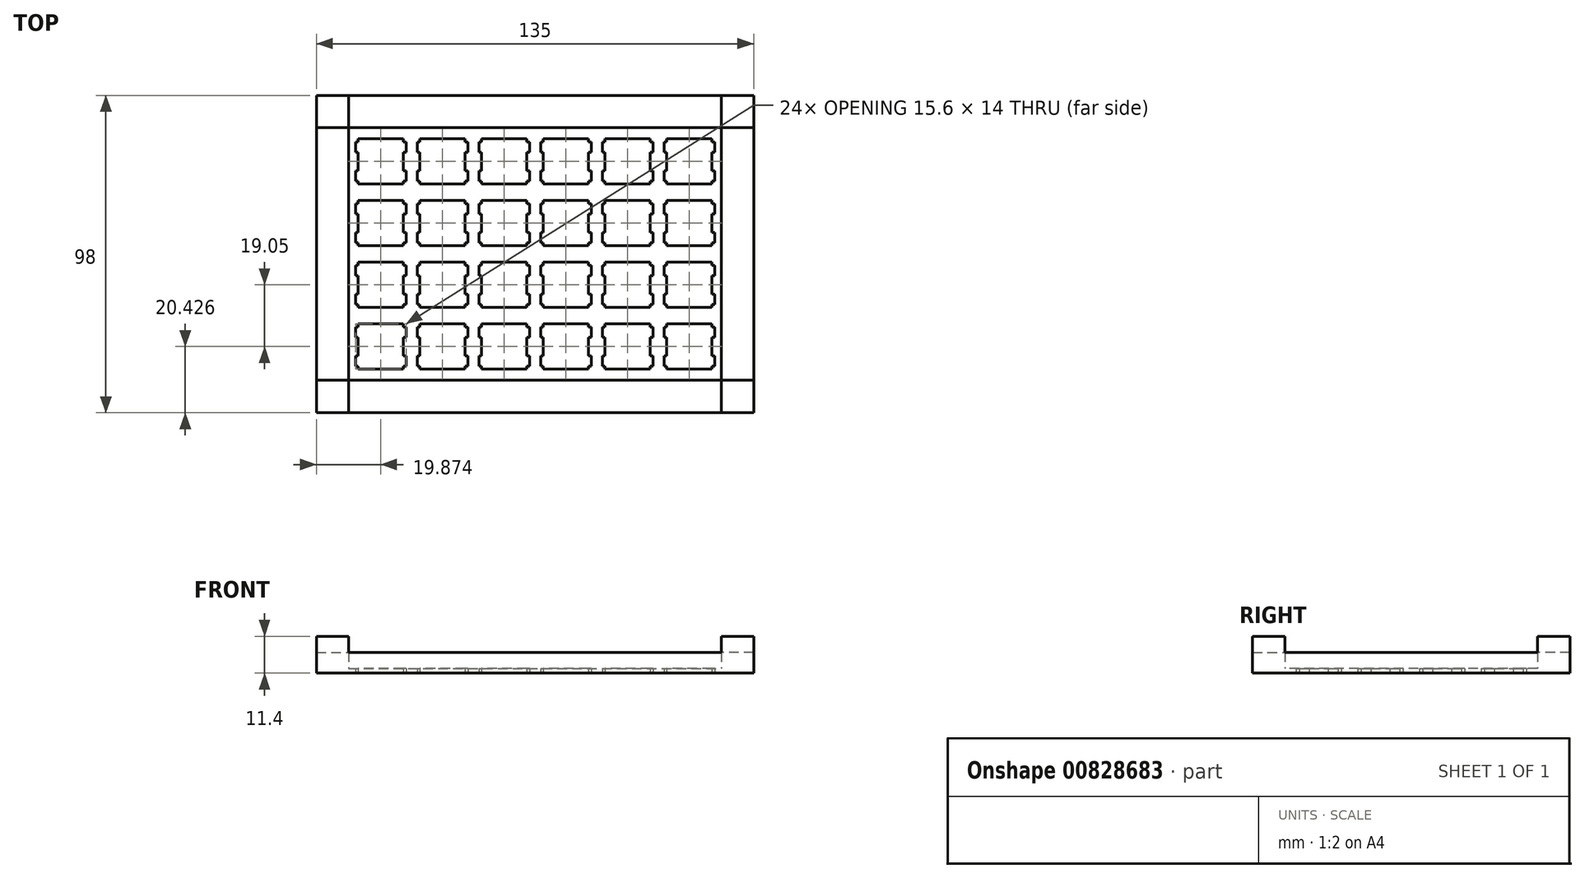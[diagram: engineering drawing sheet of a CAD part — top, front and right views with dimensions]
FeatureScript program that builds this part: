
annotation { "Feature Type Name" : "Feature", "Feature Type Description" : "" }
export const myFeature = defineFeature(function(context is Context, id is Id, definition is map)
    precondition{}
    {
        {
            var Q0;
            Q0=qCreatedBy(makeId("Top.planeOp"),FACE);
            var sketch = newSketch(context, id + "F0", { "sketchPlane" : qUnion([Q0])});
            skLineSegment(sketch, "E0", {"start": v(-60.15, 41.1) * mm, "end": v(60.15, 41.1) * mm});
            skLineSegment(sketch, "E1", {"start": v(60.15, 41.1) * mm, "end": v(60.15, -41.1) * mm});
            skLineSegment(sketch, "E2", {"start": v(60.15, -41.1) * mm, "end": v(-60.15, -41.1) * mm});
            skLineSegment(sketch, "E3", {"start": v(-60.15, -41.1) * mm, "end": v(-60.15, 41.1) * mm});
            skLineSegment(sketch, "E4", {"start": v(-54.63, -21.57) * mm, "end": v(-54.63, -22.57) * mm});
            skLineSegment(sketch, "E5", {"start": v(-54.63, -22.57) * mm, "end": v(-55.43, -22.57) * mm});
            skLineSegment(sketch, "E6", {"start": v(-55.43, -22.57) * mm, "end": v(-55.43, -25.67) * mm});
            skLineSegment(sketch, "E7", {"start": v(-55.43, -25.67) * mm, "end": v(-54.63, -25.67) * mm});
            skLineSegment(sketch, "E8", {"start": v(-54.63, -25.67) * mm, "end": v(-54.63, -31.47) * mm});
            skLineSegment(sketch, "E9", {"start": v(-54.63, -31.47) * mm, "end": v(-55.43, -31.47) * mm});
            skLineSegment(sketch, "E10", {"start": v(-55.43, -31.47) * mm, "end": v(-55.43, -34.57) * mm});
            skLineSegment(sketch, "E11", {"start": v(-55.43, -34.57) * mm, "end": v(-54.63, -34.57) * mm});
            skLineSegment(sketch, "E12", {"start": v(-54.63, -34.57) * mm, "end": v(-54.63, -35.57) * mm});
            skLineSegment(sketch, "E13", {"start": v(-54.63, -35.57) * mm, "end": v(-40.62, -35.57) * mm});
            skLineSegment(sketch, "E14", {"start": v(-40.62, -35.57) * mm, "end": v(-40.62, -34.57) * mm});
            skLineSegment(sketch, "E15", {"start": v(-40.62, -34.57) * mm, "end": v(-39.83, -34.57) * mm});
            skLineSegment(sketch, "E16", {"start": v(-39.83, -34.57) * mm, "end": v(-39.83, -31.47) * mm});
            skLineSegment(sketch, "E17", {"start": v(-39.83, -31.47) * mm, "end": v(-40.62, -31.47) * mm});
            skLineSegment(sketch, "E18", {"start": v(-40.62, -31.47) * mm, "end": v(-40.62, -25.67) * mm});
            skLineSegment(sketch, "E19", {"start": v(-40.62, -25.67) * mm, "end": v(-39.83, -25.67) * mm});
            skLineSegment(sketch, "E20", {"start": v(-39.83, -25.67) * mm, "end": v(-39.83, -22.57) * mm});
            skLineSegment(sketch, "E21", {"start": v(-39.83, -22.57) * mm, "end": v(-40.62, -22.57) * mm});
            skLineSegment(sketch, "E22", {"start": v(-40.62, -22.57) * mm, "end": v(-40.62, -21.57) * mm});
            skLineSegment(sketch, "E23", {"start": v(-40.62, -21.57) * mm, "end": v(-54.63, -21.57) * mm});
            skLineSegment(sketch, "E24", {"start": v(-35.58, -21.57) * mm, "end": v(-35.58, -22.57) * mm});
            skLineSegment(sketch, "E25", {"start": v(-35.58, -22.57) * mm, "end": v(-36.37, -22.57) * mm});
            skLineSegment(sketch, "E26", {"start": v(-36.37, -22.57) * mm, "end": v(-36.37, -25.67) * mm});
            skLineSegment(sketch, "E27", {"start": v(-36.37, -25.67) * mm, "end": v(-35.58, -25.67) * mm});
            skLineSegment(sketch, "E28", {"start": v(-35.58, -25.67) * mm, "end": v(-35.58, -31.47) * mm});
            skLineSegment(sketch, "E29", {"start": v(-35.58, -31.47) * mm, "end": v(-36.37, -31.47) * mm});
            skLineSegment(sketch, "E30", {"start": v(-36.37, -31.47) * mm, "end": v(-36.37, -34.57) * mm});
            skLineSegment(sketch, "E31", {"start": v(-36.37, -34.57) * mm, "end": v(-35.58, -34.57) * mm});
            skLineSegment(sketch, "E32", {"start": v(-35.58, -34.57) * mm, "end": v(-35.58, -35.57) * mm});
            skLineSegment(sketch, "E33", {"start": v(-35.58, -35.57) * mm, "end": v(-21.57, -35.57) * mm});
            skLineSegment(sketch, "E34", {"start": v(-21.57, -35.57) * mm, "end": v(-21.57, -34.57) * mm});
            skLineSegment(sketch, "E35", {"start": v(-21.57, -34.57) * mm, "end": v(-20.78, -34.57) * mm});
            skLineSegment(sketch, "E36", {"start": v(-20.78, -34.57) * mm, "end": v(-20.78, -31.47) * mm});
            skLineSegment(sketch, "E37", {"start": v(-20.78, -31.47) * mm, "end": v(-21.57, -31.47) * mm});
            skLineSegment(sketch, "E38", {"start": v(-21.57, -31.47) * mm, "end": v(-21.57, -25.67) * mm});
            skLineSegment(sketch, "E39", {"start": v(-21.57, -25.67) * mm, "end": v(-20.78, -25.67) * mm});
            skLineSegment(sketch, "E40", {"start": v(-20.78, -25.67) * mm, "end": v(-20.78, -22.57) * mm});
            skLineSegment(sketch, "E41", {"start": v(-20.78, -22.57) * mm, "end": v(-21.57, -22.57) * mm});
            skLineSegment(sketch, "E42", {"start": v(-21.57, -22.57) * mm, "end": v(-21.57, -21.57) * mm});
            skLineSegment(sketch, "E43", {"start": v(-21.57, -21.57) * mm, "end": v(-35.58, -21.57) * mm});
            skLineSegment(sketch, "E44", {"start": v(-16.53, -21.57) * mm, "end": v(-16.53, -22.57) * mm});
            skLineSegment(sketch, "E45", {"start": v(-16.53, -22.57) * mm, "end": v(-17.32, -22.57) * mm});
            skLineSegment(sketch, "E46", {"start": v(-17.32, -22.57) * mm, "end": v(-17.32, -25.67) * mm});
            skLineSegment(sketch, "E47", {"start": v(-17.32, -25.67) * mm, "end": v(-16.53, -25.67) * mm});
            skLineSegment(sketch, "E48", {"start": v(-16.53, -25.67) * mm, "end": v(-16.53, -31.47) * mm});
            skLineSegment(sketch, "E49", {"start": v(-16.53, -31.47) * mm, "end": v(-17.32, -31.47) * mm});
            skLineSegment(sketch, "E50", {"start": v(-17.32, -31.47) * mm, "end": v(-17.32, -34.57) * mm});
            skLineSegment(sketch, "E51", {"start": v(-17.32, -34.57) * mm, "end": v(-16.53, -34.57) * mm});
            skLineSegment(sketch, "E52", {"start": v(-16.53, -34.57) * mm, "end": v(-16.53, -35.57) * mm});
            skLineSegment(sketch, "E53", {"start": v(-16.53, -35.57) * mm, "end": v(-2.52, -35.57) * mm});
            skLineSegment(sketch, "E54", {"start": v(-2.52, -35.57) * mm, "end": v(-2.52, -34.57) * mm});
            skLineSegment(sketch, "E55", {"start": v(-2.52, -34.57) * mm, "end": v(-1.73, -34.57) * mm});
            skLineSegment(sketch, "E56", {"start": v(-1.73, -34.57) * mm, "end": v(-1.73, -31.47) * mm});
            skLineSegment(sketch, "E57", {"start": v(-1.73, -31.47) * mm, "end": v(-2.52, -31.47) * mm});
            skLineSegment(sketch, "E58", {"start": v(-2.52, -31.47) * mm, "end": v(-2.52, -25.67) * mm});
            skLineSegment(sketch, "E59", {"start": v(-2.52, -25.67) * mm, "end": v(-1.73, -25.67) * mm});
            skLineSegment(sketch, "E60", {"start": v(-1.73, -25.67) * mm, "end": v(-1.73, -22.57) * mm});
            skLineSegment(sketch, "E61", {"start": v(-1.73, -22.57) * mm, "end": v(-2.52, -22.57) * mm});
            skLineSegment(sketch, "E62", {"start": v(-2.52, -22.57) * mm, "end": v(-2.52, -21.57) * mm});
            skLineSegment(sketch, "E63", {"start": v(-2.52, -21.57) * mm, "end": v(-16.53, -21.57) * mm});
            skLineSegment(sketch, "E64", {"start": v(2.52, -21.57) * mm, "end": v(2.52, -22.57) * mm});
            skLineSegment(sketch, "E65", {"start": v(2.52, -22.57) * mm, "end": v(1.73, -22.57) * mm});
            skLineSegment(sketch, "E66", {"start": v(1.73, -22.57) * mm, "end": v(1.73, -25.67) * mm});
            skLineSegment(sketch, "E67", {"start": v(1.73, -25.67) * mm, "end": v(2.52, -25.67) * mm});
            skLineSegment(sketch, "E68", {"start": v(2.52, -25.67) * mm, "end": v(2.52, -31.47) * mm});
            skLineSegment(sketch, "E69", {"start": v(2.52, -31.47) * mm, "end": v(1.73, -31.47) * mm});
            skLineSegment(sketch, "E70", {"start": v(1.73, -31.47) * mm, "end": v(1.73, -34.57) * mm});
            skLineSegment(sketch, "E71", {"start": v(1.73, -34.57) * mm, "end": v(2.52, -34.57) * mm});
            skLineSegment(sketch, "E72", {"start": v(2.52, -34.57) * mm, "end": v(2.52, -35.57) * mm});
            skLineSegment(sketch, "E73", {"start": v(2.52, -35.57) * mm, "end": v(16.53, -35.57) * mm});
            skLineSegment(sketch, "E74", {"start": v(16.53, -35.57) * mm, "end": v(16.53, -34.57) * mm});
            skLineSegment(sketch, "E75", {"start": v(16.53, -34.57) * mm, "end": v(17.32, -34.57) * mm});
            skLineSegment(sketch, "E76", {"start": v(17.32, -34.57) * mm, "end": v(17.32, -31.47) * mm});
            skLineSegment(sketch, "E77", {"start": v(17.32, -31.47) * mm, "end": v(16.53, -31.47) * mm});
            skLineSegment(sketch, "E78", {"start": v(16.53, -31.47) * mm, "end": v(16.53, -25.67) * mm});
            skLineSegment(sketch, "E79", {"start": v(16.53, -25.67) * mm, "end": v(17.32, -25.67) * mm});
            skLineSegment(sketch, "E80", {"start": v(17.32, -25.67) * mm, "end": v(17.32, -22.57) * mm});
            skLineSegment(sketch, "E81", {"start": v(17.32, -22.57) * mm, "end": v(16.53, -22.57) * mm});
            skLineSegment(sketch, "E82", {"start": v(16.53, -22.57) * mm, "end": v(16.53, -21.57) * mm});
            skLineSegment(sketch, "E83", {"start": v(16.53, -21.57) * mm, "end": v(2.52, -21.57) * mm});
            skLineSegment(sketch, "E84", {"start": v(21.57, -21.57) * mm, "end": v(21.57, -22.57) * mm});
            skLineSegment(sketch, "E85", {"start": v(21.57, -22.57) * mm, "end": v(20.78, -22.57) * mm});
            skLineSegment(sketch, "E86", {"start": v(20.78, -22.57) * mm, "end": v(20.78, -25.67) * mm});
            skLineSegment(sketch, "E87", {"start": v(20.78, -25.67) * mm, "end": v(21.57, -25.67) * mm});
            skLineSegment(sketch, "E88", {"start": v(21.57, -25.67) * mm, "end": v(21.57, -31.47) * mm});
            skLineSegment(sketch, "E89", {"start": v(21.57, -31.47) * mm, "end": v(20.78, -31.47) * mm});
            skLineSegment(sketch, "E90", {"start": v(20.78, -31.47) * mm, "end": v(20.78, -34.57) * mm});
            skLineSegment(sketch, "E91", {"start": v(20.78, -34.57) * mm, "end": v(21.57, -34.57) * mm});
            skLineSegment(sketch, "E92", {"start": v(21.57, -34.57) * mm, "end": v(21.57, -35.57) * mm});
            skLineSegment(sketch, "E93", {"start": v(21.57, -35.57) * mm, "end": v(35.58, -35.57) * mm});
            skLineSegment(sketch, "E94", {"start": v(35.58, -35.57) * mm, "end": v(35.58, -34.57) * mm});
            skLineSegment(sketch, "E95", {"start": v(35.58, -34.57) * mm, "end": v(36.37, -34.57) * mm});
            skLineSegment(sketch, "E96", {"start": v(36.37, -34.57) * mm, "end": v(36.37, -31.47) * mm});
            skLineSegment(sketch, "E97", {"start": v(36.37, -31.47) * mm, "end": v(35.58, -31.47) * mm});
            skLineSegment(sketch, "E98", {"start": v(35.58, -31.47) * mm, "end": v(35.58, -25.67) * mm});
            skLineSegment(sketch, "E99", {"start": v(35.58, -25.67) * mm, "end": v(36.37, -25.67) * mm});
            skLineSegment(sketch, "E100", {"start": v(36.37, -25.67) * mm, "end": v(36.37, -22.57) * mm});
            skLineSegment(sketch, "E101", {"start": v(36.37, -22.57) * mm, "end": v(35.58, -22.57) * mm});
            skLineSegment(sketch, "E102", {"start": v(35.58, -22.57) * mm, "end": v(35.58, -21.57) * mm});
            skLineSegment(sketch, "E103", {"start": v(35.58, -21.57) * mm, "end": v(21.57, -21.57) * mm});
            skLineSegment(sketch, "E104", {"start": v(40.62, -21.57) * mm, "end": v(40.62, -22.57) * mm});
            skLineSegment(sketch, "E105", {"start": v(40.62, -22.57) * mm, "end": v(39.83, -22.57) * mm});
            skLineSegment(sketch, "E106", {"start": v(39.83, -22.57) * mm, "end": v(39.83, -25.67) * mm});
            skLineSegment(sketch, "E107", {"start": v(39.83, -25.67) * mm, "end": v(40.62, -25.67) * mm});
            skLineSegment(sketch, "E108", {"start": v(40.62, -25.67) * mm, "end": v(40.62, -31.47) * mm});
            skLineSegment(sketch, "E109", {"start": v(40.62, -31.47) * mm, "end": v(39.83, -31.47) * mm});
            skLineSegment(sketch, "E110", {"start": v(39.83, -31.47) * mm, "end": v(39.83, -34.57) * mm});
            skLineSegment(sketch, "E111", {"start": v(39.83, -34.57) * mm, "end": v(40.62, -34.57) * mm});
            skLineSegment(sketch, "E112", {"start": v(40.62, -34.57) * mm, "end": v(40.62, -35.57) * mm});
            skLineSegment(sketch, "E113", {"start": v(40.62, -35.57) * mm, "end": v(54.62, -35.57) * mm});
            skLineSegment(sketch, "E114", {"start": v(54.62, -35.57) * mm, "end": v(54.62, -34.57) * mm});
            skLineSegment(sketch, "E115", {"start": v(54.62, -34.57) * mm, "end": v(55.42, -34.57) * mm});
            skLineSegment(sketch, "E116", {"start": v(55.42, -34.57) * mm, "end": v(55.42, -31.47) * mm});
            skLineSegment(sketch, "E117", {"start": v(55.42, -31.47) * mm, "end": v(54.62, -31.47) * mm});
            skLineSegment(sketch, "E118", {"start": v(54.62, -31.47) * mm, "end": v(54.62, -25.67) * mm});
            skLineSegment(sketch, "E119", {"start": v(54.62, -25.67) * mm, "end": v(55.42, -25.67) * mm});
            skLineSegment(sketch, "E120", {"start": v(55.42, -25.67) * mm, "end": v(55.42, -22.57) * mm});
            skLineSegment(sketch, "E121", {"start": v(55.42, -22.57) * mm, "end": v(54.62, -22.57) * mm});
            skLineSegment(sketch, "E122", {"start": v(54.62, -22.57) * mm, "end": v(54.62, -21.57) * mm});
            skLineSegment(sketch, "E123", {"start": v(54.62, -21.57) * mm, "end": v(40.62, -21.57) * mm});
            skLineSegment(sketch, "E124", {"start": v(-54.63, -2.52) * mm, "end": v(-54.63, -3.52) * mm});
            skLineSegment(sketch, "E125", {"start": v(-54.63, -3.52) * mm, "end": v(-55.43, -3.52) * mm});
            skLineSegment(sketch, "E126", {"start": v(-55.43, -3.52) * mm, "end": v(-55.43, -6.62) * mm});
            skLineSegment(sketch, "E127", {"start": v(-55.43, -6.62) * mm, "end": v(-54.63, -6.62) * mm});
            skLineSegment(sketch, "E128", {"start": v(-54.63, -6.62) * mm, "end": v(-54.63, -12.42) * mm});
            skLineSegment(sketch, "E129", {"start": v(-54.63, -12.42) * mm, "end": v(-55.43, -12.42) * mm});
            skLineSegment(sketch, "E130", {"start": v(-55.43, -12.42) * mm, "end": v(-55.43, -15.52) * mm});
            skLineSegment(sketch, "E131", {"start": v(-55.43, -15.52) * mm, "end": v(-54.63, -15.52) * mm});
            skLineSegment(sketch, "E132", {"start": v(-54.63, -15.52) * mm, "end": v(-54.63, -16.52) * mm});
            skLineSegment(sketch, "E133", {"start": v(-54.63, -16.52) * mm, "end": v(-40.62, -16.52) * mm});
            skLineSegment(sketch, "E134", {"start": v(-40.62, -16.52) * mm, "end": v(-40.62, -15.52) * mm});
            skLineSegment(sketch, "E135", {"start": v(-40.62, -15.52) * mm, "end": v(-39.83, -15.52) * mm});
            skLineSegment(sketch, "E136", {"start": v(-39.83, -15.52) * mm, "end": v(-39.83, -12.42) * mm});
            skLineSegment(sketch, "E137", {"start": v(-39.83, -12.42) * mm, "end": v(-40.62, -12.42) * mm});
            skLineSegment(sketch, "E138", {"start": v(-40.62, -12.42) * mm, "end": v(-40.62, -6.62) * mm});
            skLineSegment(sketch, "E139", {"start": v(-40.62, -6.62) * mm, "end": v(-39.83, -6.62) * mm});
            skLineSegment(sketch, "E140", {"start": v(-39.83, -6.62) * mm, "end": v(-39.83, -3.52) * mm});
            skLineSegment(sketch, "E141", {"start": v(-39.83, -3.52) * mm, "end": v(-40.62, -3.52) * mm});
            skLineSegment(sketch, "E142", {"start": v(-40.62, -3.52) * mm, "end": v(-40.62, -2.52) * mm});
            skLineSegment(sketch, "E143", {"start": v(-40.62, -2.52) * mm, "end": v(-54.63, -2.52) * mm});
            skLineSegment(sketch, "E144", {"start": v(-35.58, -2.52) * mm, "end": v(-35.58, -3.52) * mm});
            skLineSegment(sketch, "E145", {"start": v(-35.58, -3.52) * mm, "end": v(-36.37, -3.52) * mm});
            skLineSegment(sketch, "E146", {"start": v(-36.37, -3.52) * mm, "end": v(-36.37, -6.62) * mm});
            skLineSegment(sketch, "E147", {"start": v(-36.37, -6.62) * mm, "end": v(-35.58, -6.62) * mm});
            skLineSegment(sketch, "E148", {"start": v(-35.58, -6.62) * mm, "end": v(-35.58, -12.42) * mm});
            skLineSegment(sketch, "E149", {"start": v(-35.58, -12.42) * mm, "end": v(-36.37, -12.42) * mm});
            skLineSegment(sketch, "E150", {"start": v(-36.37, -12.42) * mm, "end": v(-36.37, -15.52) * mm});
            skLineSegment(sketch, "E151", {"start": v(-36.37, -15.52) * mm, "end": v(-35.58, -15.52) * mm});
            skLineSegment(sketch, "E152", {"start": v(-35.58, -15.52) * mm, "end": v(-35.58, -16.52) * mm});
            skLineSegment(sketch, "E153", {"start": v(-35.58, -16.52) * mm, "end": v(-21.57, -16.52) * mm});
            skLineSegment(sketch, "E154", {"start": v(-21.57, -16.52) * mm, "end": v(-21.57, -15.52) * mm});
            skLineSegment(sketch, "E155", {"start": v(-21.57, -15.52) * mm, "end": v(-20.78, -15.52) * mm});
            skLineSegment(sketch, "E156", {"start": v(-20.78, -15.52) * mm, "end": v(-20.78, -12.42) * mm});
            skLineSegment(sketch, "E157", {"start": v(-20.78, -12.42) * mm, "end": v(-21.57, -12.42) * mm});
            skLineSegment(sketch, "E158", {"start": v(-21.57, -12.42) * mm, "end": v(-21.57, -6.62) * mm});
            skLineSegment(sketch, "E159", {"start": v(-21.57, -6.62) * mm, "end": v(-20.78, -6.62) * mm});
            skLineSegment(sketch, "E160", {"start": v(-20.78, -6.62) * mm, "end": v(-20.78, -3.52) * mm});
            skLineSegment(sketch, "E161", {"start": v(-20.78, -3.52) * mm, "end": v(-21.57, -3.52) * mm});
            skLineSegment(sketch, "E162", {"start": v(-21.57, -3.52) * mm, "end": v(-21.57, -2.52) * mm});
            skLineSegment(sketch, "E163", {"start": v(-21.57, -2.52) * mm, "end": v(-35.58, -2.52) * mm});
            skLineSegment(sketch, "E164", {"start": v(-16.53, -2.52) * mm, "end": v(-16.53, -3.52) * mm});
            skLineSegment(sketch, "E165", {"start": v(-16.53, -3.52) * mm, "end": v(-17.32, -3.52) * mm});
            skLineSegment(sketch, "E166", {"start": v(-17.32, -3.52) * mm, "end": v(-17.32, -6.62) * mm});
            skLineSegment(sketch, "E167", {"start": v(-17.32, -6.62) * mm, "end": v(-16.53, -6.62) * mm});
            skLineSegment(sketch, "E168", {"start": v(-16.53, -6.62) * mm, "end": v(-16.53, -12.42) * mm});
            skLineSegment(sketch, "E169", {"start": v(-16.53, -12.42) * mm, "end": v(-17.32, -12.42) * mm});
            skLineSegment(sketch, "E170", {"start": v(-17.32, -12.42) * mm, "end": v(-17.32, -15.52) * mm});
            skLineSegment(sketch, "E171", {"start": v(-17.32, -15.52) * mm, "end": v(-16.53, -15.52) * mm});
            skLineSegment(sketch, "E172", {"start": v(-16.53, -15.52) * mm, "end": v(-16.53, -16.52) * mm});
            skLineSegment(sketch, "E173", {"start": v(-16.53, -16.52) * mm, "end": v(-2.52, -16.52) * mm});
            skLineSegment(sketch, "E174", {"start": v(-2.52, -16.52) * mm, "end": v(-2.52, -15.52) * mm});
            skLineSegment(sketch, "E175", {"start": v(-2.52, -15.52) * mm, "end": v(-1.73, -15.52) * mm});
            skLineSegment(sketch, "E176", {"start": v(-1.73, -15.52) * mm, "end": v(-1.73, -12.42) * mm});
            skLineSegment(sketch, "E177", {"start": v(-1.73, -12.42) * mm, "end": v(-2.52, -12.42) * mm});
            skLineSegment(sketch, "E178", {"start": v(-2.52, -12.42) * mm, "end": v(-2.52, -6.62) * mm});
            skLineSegment(sketch, "E179", {"start": v(-2.52, -6.62) * mm, "end": v(-1.73, -6.62) * mm});
            skLineSegment(sketch, "E180", {"start": v(-1.73, -6.62) * mm, "end": v(-1.73, -3.52) * mm});
            skLineSegment(sketch, "E181", {"start": v(-1.73, -3.52) * mm, "end": v(-2.52, -3.52) * mm});
            skLineSegment(sketch, "E182", {"start": v(-2.52, -3.52) * mm, "end": v(-2.52, -2.52) * mm});
            skLineSegment(sketch, "E183", {"start": v(-2.52, -2.52) * mm, "end": v(-16.53, -2.52) * mm});
            skLineSegment(sketch, "E184", {"start": v(2.52, -2.52) * mm, "end": v(2.52, -3.52) * mm});
            skLineSegment(sketch, "E185", {"start": v(2.52, -3.52) * mm, "end": v(1.73, -3.52) * mm});
            skLineSegment(sketch, "E186", {"start": v(1.73, -3.52) * mm, "end": v(1.73, -6.62) * mm});
            skLineSegment(sketch, "E187", {"start": v(1.73, -6.62) * mm, "end": v(2.52, -6.62) * mm});
            skLineSegment(sketch, "E188", {"start": v(2.52, -6.62) * mm, "end": v(2.52, -12.42) * mm});
            skLineSegment(sketch, "E189", {"start": v(2.52, -12.42) * mm, "end": v(1.73, -12.42) * mm});
            skLineSegment(sketch, "E190", {"start": v(1.73, -12.42) * mm, "end": v(1.73, -15.52) * mm});
            skLineSegment(sketch, "E191", {"start": v(1.73, -15.52) * mm, "end": v(2.52, -15.52) * mm});
            skLineSegment(sketch, "E192", {"start": v(2.52, -15.52) * mm, "end": v(2.52, -16.52) * mm});
            skLineSegment(sketch, "E193", {"start": v(2.52, -16.52) * mm, "end": v(16.53, -16.52) * mm});
            skLineSegment(sketch, "E194", {"start": v(16.53, -16.52) * mm, "end": v(16.53, -15.52) * mm});
            skLineSegment(sketch, "E195", {"start": v(16.53, -15.52) * mm, "end": v(17.32, -15.52) * mm});
            skLineSegment(sketch, "E196", {"start": v(17.32, -15.52) * mm, "end": v(17.32, -12.42) * mm});
            skLineSegment(sketch, "E197", {"start": v(17.32, -12.42) * mm, "end": v(16.53, -12.42) * mm});
            skLineSegment(sketch, "E198", {"start": v(16.53, -12.42) * mm, "end": v(16.53, -6.62) * mm});
            skLineSegment(sketch, "E199", {"start": v(16.53, -6.62) * mm, "end": v(17.32, -6.62) * mm});
            skLineSegment(sketch, "E200", {"start": v(17.32, -6.62) * mm, "end": v(17.32, -3.52) * mm});
            skLineSegment(sketch, "E201", {"start": v(17.32, -3.52) * mm, "end": v(16.53, -3.52) * mm});
            skLineSegment(sketch, "E202", {"start": v(16.53, -3.52) * mm, "end": v(16.53, -2.52) * mm});
            skLineSegment(sketch, "E203", {"start": v(16.53, -2.52) * mm, "end": v(2.52, -2.52) * mm});
            skLineSegment(sketch, "E204", {"start": v(21.57, -2.52) * mm, "end": v(21.57, -3.52) * mm});
            skLineSegment(sketch, "E205", {"start": v(21.57, -3.52) * mm, "end": v(20.78, -3.52) * mm});
            skLineSegment(sketch, "E206", {"start": v(20.78, -3.52) * mm, "end": v(20.78, -6.62) * mm});
            skLineSegment(sketch, "E207", {"start": v(20.78, -6.62) * mm, "end": v(21.57, -6.62) * mm});
            skLineSegment(sketch, "E208", {"start": v(21.57, -6.62) * mm, "end": v(21.57, -12.42) * mm});
            skLineSegment(sketch, "E209", {"start": v(21.57, -12.42) * mm, "end": v(20.78, -12.42) * mm});
            skLineSegment(sketch, "E210", {"start": v(20.78, -12.42) * mm, "end": v(20.78, -15.52) * mm});
            skLineSegment(sketch, "E211", {"start": v(20.78, -15.52) * mm, "end": v(21.57, -15.52) * mm});
            skLineSegment(sketch, "E212", {"start": v(21.57, -15.52) * mm, "end": v(21.57, -16.52) * mm});
            skLineSegment(sketch, "E213", {"start": v(21.57, -16.52) * mm, "end": v(35.58, -16.52) * mm});
            skLineSegment(sketch, "E214", {"start": v(35.58, -16.52) * mm, "end": v(35.58, -15.52) * mm});
            skLineSegment(sketch, "E215", {"start": v(35.58, -15.52) * mm, "end": v(36.37, -15.52) * mm});
            skLineSegment(sketch, "E216", {"start": v(36.37, -15.52) * mm, "end": v(36.37, -12.42) * mm});
            skLineSegment(sketch, "E217", {"start": v(36.37, -12.42) * mm, "end": v(35.58, -12.42) * mm});
            skLineSegment(sketch, "E218", {"start": v(35.58, -12.42) * mm, "end": v(35.58, -6.62) * mm});
            skLineSegment(sketch, "E219", {"start": v(35.58, -6.62) * mm, "end": v(36.37, -6.62) * mm});
            skLineSegment(sketch, "E220", {"start": v(36.37, -6.62) * mm, "end": v(36.37, -3.52) * mm});
            skLineSegment(sketch, "E221", {"start": v(36.37, -3.52) * mm, "end": v(35.58, -3.52) * mm});
            skLineSegment(sketch, "E222", {"start": v(35.58, -3.52) * mm, "end": v(35.58, -2.52) * mm});
            skLineSegment(sketch, "E223", {"start": v(35.58, -2.52) * mm, "end": v(21.57, -2.52) * mm});
            skLineSegment(sketch, "E224", {"start": v(40.62, -2.52) * mm, "end": v(40.62, -3.52) * mm});
            skLineSegment(sketch, "E225", {"start": v(40.62, -3.52) * mm, "end": v(39.83, -3.52) * mm});
            skLineSegment(sketch, "E226", {"start": v(39.83, -3.52) * mm, "end": v(39.83, -6.62) * mm});
            skLineSegment(sketch, "E227", {"start": v(39.83, -6.62) * mm, "end": v(40.62, -6.62) * mm});
            skLineSegment(sketch, "E228", {"start": v(40.62, -6.62) * mm, "end": v(40.62, -12.42) * mm});
            skLineSegment(sketch, "E229", {"start": v(40.62, -12.42) * mm, "end": v(39.83, -12.42) * mm});
            skLineSegment(sketch, "E230", {"start": v(39.83, -12.42) * mm, "end": v(39.83, -15.52) * mm});
            skLineSegment(sketch, "E231", {"start": v(39.83, -15.52) * mm, "end": v(40.62, -15.52) * mm});
            skLineSegment(sketch, "E232", {"start": v(40.62, -15.52) * mm, "end": v(40.62, -16.52) * mm});
            skLineSegment(sketch, "E233", {"start": v(40.62, -16.52) * mm, "end": v(54.62, -16.52) * mm});
            skLineSegment(sketch, "E234", {"start": v(54.62, -16.52) * mm, "end": v(54.62, -15.52) * mm});
            skLineSegment(sketch, "E235", {"start": v(54.62, -15.52) * mm, "end": v(55.42, -15.52) * mm});
            skLineSegment(sketch, "E236", {"start": v(55.42, -15.52) * mm, "end": v(55.42, -12.42) * mm});
            skLineSegment(sketch, "E237", {"start": v(55.42, -12.42) * mm, "end": v(54.62, -12.42) * mm});
            skLineSegment(sketch, "E238", {"start": v(54.62, -12.42) * mm, "end": v(54.62, -6.62) * mm});
            skLineSegment(sketch, "E239", {"start": v(54.62, -6.62) * mm, "end": v(55.42, -6.62) * mm});
            skLineSegment(sketch, "E240", {"start": v(55.42, -6.62) * mm, "end": v(55.42, -3.52) * mm});
            skLineSegment(sketch, "E241", {"start": v(55.42, -3.52) * mm, "end": v(54.62, -3.52) * mm});
            skLineSegment(sketch, "E242", {"start": v(54.62, -3.52) * mm, "end": v(54.62, -2.52) * mm});
            skLineSegment(sketch, "E243", {"start": v(54.62, -2.52) * mm, "end": v(40.62, -2.52) * mm});
            skLineSegment(sketch, "E244", {"start": v(-54.63, 16.53) * mm, "end": v(-54.63, 15.53) * mm});
            skLineSegment(sketch, "E245", {"start": v(-54.63, 15.53) * mm, "end": v(-55.43, 15.53) * mm});
            skLineSegment(sketch, "E246", {"start": v(-55.43, 15.53) * mm, "end": v(-55.43, 12.43) * mm});
            skLineSegment(sketch, "E247", {"start": v(-55.43, 12.43) * mm, "end": v(-54.63, 12.43) * mm});
            skLineSegment(sketch, "E248", {"start": v(-54.63, 12.43) * mm, "end": v(-54.63, 6.63) * mm});
            skLineSegment(sketch, "E249", {"start": v(-54.63, 6.63) * mm, "end": v(-55.43, 6.63) * mm});
            skLineSegment(sketch, "E250", {"start": v(-55.43, 6.63) * mm, "end": v(-55.43, 3.53) * mm});
            skLineSegment(sketch, "E251", {"start": v(-55.43, 3.53) * mm, "end": v(-54.63, 3.53) * mm});
            skLineSegment(sketch, "E252", {"start": v(-54.63, 3.53) * mm, "end": v(-54.63, 2.53) * mm});
            skLineSegment(sketch, "E253", {"start": v(-54.63, 2.53) * mm, "end": v(-40.62, 2.53) * mm});
            skLineSegment(sketch, "E254", {"start": v(-40.62, 2.53) * mm, "end": v(-40.62, 3.53) * mm});
            skLineSegment(sketch, "E255", {"start": v(-40.62, 3.53) * mm, "end": v(-39.83, 3.53) * mm});
            skLineSegment(sketch, "E256", {"start": v(-39.83, 3.53) * mm, "end": v(-39.83, 6.63) * mm});
            skLineSegment(sketch, "E257", {"start": v(-39.83, 6.63) * mm, "end": v(-40.62, 6.63) * mm});
            skLineSegment(sketch, "E258", {"start": v(-40.62, 6.63) * mm, "end": v(-40.62, 12.43) * mm});
            skLineSegment(sketch, "E259", {"start": v(-40.62, 12.43) * mm, "end": v(-39.83, 12.43) * mm});
            skLineSegment(sketch, "E260", {"start": v(-39.83, 12.43) * mm, "end": v(-39.83, 15.53) * mm});
            skLineSegment(sketch, "E261", {"start": v(-39.83, 15.53) * mm, "end": v(-40.62, 15.53) * mm});
            skLineSegment(sketch, "E262", {"start": v(-40.62, 15.53) * mm, "end": v(-40.62, 16.53) * mm});
            skLineSegment(sketch, "E263", {"start": v(-40.62, 16.53) * mm, "end": v(-54.63, 16.53) * mm});
            skLineSegment(sketch, "E264", {"start": v(-35.58, 16.53) * mm, "end": v(-35.58, 15.53) * mm});
            skLineSegment(sketch, "E265", {"start": v(-35.58, 15.53) * mm, "end": v(-36.37, 15.53) * mm});
            skLineSegment(sketch, "E266", {"start": v(-36.37, 15.53) * mm, "end": v(-36.37, 12.43) * mm});
            skLineSegment(sketch, "E267", {"start": v(-36.37, 12.43) * mm, "end": v(-35.58, 12.43) * mm});
            skLineSegment(sketch, "E268", {"start": v(-35.58, 12.43) * mm, "end": v(-35.58, 6.63) * mm});
            skLineSegment(sketch, "E269", {"start": v(-35.58, 6.63) * mm, "end": v(-36.37, 6.63) * mm});
            skLineSegment(sketch, "E270", {"start": v(-36.37, 6.63) * mm, "end": v(-36.37, 3.53) * mm});
            skLineSegment(sketch, "E271", {"start": v(-36.37, 3.53) * mm, "end": v(-35.58, 3.53) * mm});
            skLineSegment(sketch, "E272", {"start": v(-35.58, 3.53) * mm, "end": v(-35.58, 2.53) * mm});
            skLineSegment(sketch, "E273", {"start": v(-35.58, 2.53) * mm, "end": v(-21.57, 2.53) * mm});
            skLineSegment(sketch, "E274", {"start": v(-21.57, 2.53) * mm, "end": v(-21.57, 3.53) * mm});
            skLineSegment(sketch, "E275", {"start": v(-21.57, 3.53) * mm, "end": v(-20.78, 3.53) * mm});
            skLineSegment(sketch, "E276", {"start": v(-20.78, 3.53) * mm, "end": v(-20.78, 6.63) * mm});
            skLineSegment(sketch, "E277", {"start": v(-20.78, 6.63) * mm, "end": v(-21.57, 6.63) * mm});
            skLineSegment(sketch, "E278", {"start": v(-21.57, 6.63) * mm, "end": v(-21.57, 12.43) * mm});
            skLineSegment(sketch, "E279", {"start": v(-21.57, 12.43) * mm, "end": v(-20.78, 12.43) * mm});
            skLineSegment(sketch, "E280", {"start": v(-20.78, 12.43) * mm, "end": v(-20.78, 15.53) * mm});
            skLineSegment(sketch, "E281", {"start": v(-20.78, 15.53) * mm, "end": v(-21.57, 15.53) * mm});
            skLineSegment(sketch, "E282", {"start": v(-21.57, 15.53) * mm, "end": v(-21.57, 16.53) * mm});
            skLineSegment(sketch, "E283", {"start": v(-21.57, 16.53) * mm, "end": v(-35.58, 16.53) * mm});
            skLineSegment(sketch, "E284", {"start": v(-16.53, 16.53) * mm, "end": v(-16.53, 15.53) * mm});
            skLineSegment(sketch, "E285", {"start": v(-16.53, 15.53) * mm, "end": v(-17.32, 15.53) * mm});
            skLineSegment(sketch, "E286", {"start": v(-17.32, 15.53) * mm, "end": v(-17.32, 12.43) * mm});
            skLineSegment(sketch, "E287", {"start": v(-17.32, 12.43) * mm, "end": v(-16.53, 12.43) * mm});
            skLineSegment(sketch, "E288", {"start": v(-16.53, 12.43) * mm, "end": v(-16.53, 6.63) * mm});
            skLineSegment(sketch, "E289", {"start": v(-16.53, 6.63) * mm, "end": v(-17.32, 6.63) * mm});
            skLineSegment(sketch, "E290", {"start": v(-17.32, 6.63) * mm, "end": v(-17.32, 3.53) * mm});
            skLineSegment(sketch, "E291", {"start": v(-17.32, 3.53) * mm, "end": v(-16.53, 3.53) * mm});
            skLineSegment(sketch, "E292", {"start": v(-16.53, 3.53) * mm, "end": v(-16.53, 2.53) * mm});
            skLineSegment(sketch, "E293", {"start": v(-16.53, 2.53) * mm, "end": v(-2.52, 2.53) * mm});
            skLineSegment(sketch, "E294", {"start": v(-2.52, 2.53) * mm, "end": v(-2.52, 3.53) * mm});
            skLineSegment(sketch, "E295", {"start": v(-2.52, 3.53) * mm, "end": v(-1.73, 3.53) * mm});
            skLineSegment(sketch, "E296", {"start": v(-1.73, 3.53) * mm, "end": v(-1.73, 6.63) * mm});
            skLineSegment(sketch, "E297", {"start": v(-1.73, 6.63) * mm, "end": v(-2.52, 6.63) * mm});
            skLineSegment(sketch, "E298", {"start": v(-2.52, 6.63) * mm, "end": v(-2.52, 12.43) * mm});
            skLineSegment(sketch, "E299", {"start": v(-2.52, 12.43) * mm, "end": v(-1.73, 12.43) * mm});
            skLineSegment(sketch, "E300", {"start": v(-1.73, 12.43) * mm, "end": v(-1.73, 15.53) * mm});
            skLineSegment(sketch, "E301", {"start": v(-1.73, 15.53) * mm, "end": v(-2.52, 15.53) * mm});
            skLineSegment(sketch, "E302", {"start": v(-2.52, 15.53) * mm, "end": v(-2.52, 16.53) * mm});
            skLineSegment(sketch, "E303", {"start": v(-2.52, 16.53) * mm, "end": v(-16.53, 16.53) * mm});
            skLineSegment(sketch, "E304", {"start": v(2.52, 16.53) * mm, "end": v(2.52, 15.53) * mm});
            skLineSegment(sketch, "E305", {"start": v(2.52, 15.53) * mm, "end": v(1.73, 15.53) * mm});
            skLineSegment(sketch, "E306", {"start": v(1.73, 15.53) * mm, "end": v(1.73, 12.43) * mm});
            skLineSegment(sketch, "E307", {"start": v(1.73, 12.43) * mm, "end": v(2.52, 12.43) * mm});
            skLineSegment(sketch, "E308", {"start": v(2.52, 12.43) * mm, "end": v(2.52, 6.63) * mm});
            skLineSegment(sketch, "E309", {"start": v(2.52, 6.63) * mm, "end": v(1.73, 6.63) * mm});
            skLineSegment(sketch, "E310", {"start": v(1.73, 6.63) * mm, "end": v(1.73, 3.53) * mm});
            skLineSegment(sketch, "E311", {"start": v(1.73, 3.53) * mm, "end": v(2.52, 3.53) * mm});
            skLineSegment(sketch, "E312", {"start": v(2.52, 3.53) * mm, "end": v(2.52, 2.53) * mm});
            skLineSegment(sketch, "E313", {"start": v(2.52, 2.53) * mm, "end": v(16.53, 2.53) * mm});
            skLineSegment(sketch, "E314", {"start": v(16.53, 2.53) * mm, "end": v(16.53, 3.53) * mm});
            skLineSegment(sketch, "E315", {"start": v(16.53, 3.53) * mm, "end": v(17.32, 3.53) * mm});
            skLineSegment(sketch, "E316", {"start": v(17.32, 3.53) * mm, "end": v(17.32, 6.63) * mm});
            skLineSegment(sketch, "E317", {"start": v(17.32, 6.63) * mm, "end": v(16.53, 6.63) * mm});
            skLineSegment(sketch, "E318", {"start": v(16.53, 6.63) * mm, "end": v(16.53, 12.43) * mm});
            skLineSegment(sketch, "E319", {"start": v(16.53, 12.43) * mm, "end": v(17.32, 12.43) * mm});
            skLineSegment(sketch, "E320", {"start": v(17.32, 12.43) * mm, "end": v(17.32, 15.53) * mm});
            skLineSegment(sketch, "E321", {"start": v(17.32, 15.53) * mm, "end": v(16.53, 15.53) * mm});
            skLineSegment(sketch, "E322", {"start": v(16.53, 15.53) * mm, "end": v(16.53, 16.53) * mm});
            skLineSegment(sketch, "E323", {"start": v(16.53, 16.53) * mm, "end": v(2.52, 16.53) * mm});
            skLineSegment(sketch, "E324", {"start": v(21.57, 16.53) * mm, "end": v(21.57, 15.53) * mm});
            skLineSegment(sketch, "E325", {"start": v(21.57, 15.53) * mm, "end": v(20.78, 15.53) * mm});
            skLineSegment(sketch, "E326", {"start": v(20.78, 15.53) * mm, "end": v(20.78, 12.43) * mm});
            skLineSegment(sketch, "E327", {"start": v(20.78, 12.43) * mm, "end": v(21.57, 12.43) * mm});
            skLineSegment(sketch, "E328", {"start": v(21.57, 12.43) * mm, "end": v(21.57, 6.63) * mm});
            skLineSegment(sketch, "E329", {"start": v(21.57, 6.63) * mm, "end": v(20.78, 6.63) * mm});
            skLineSegment(sketch, "E330", {"start": v(20.78, 6.63) * mm, "end": v(20.78, 3.53) * mm});
            skLineSegment(sketch, "E331", {"start": v(20.78, 3.53) * mm, "end": v(21.57, 3.53) * mm});
            skLineSegment(sketch, "E332", {"start": v(21.57, 3.53) * mm, "end": v(21.57, 2.53) * mm});
            skLineSegment(sketch, "E333", {"start": v(21.57, 2.53) * mm, "end": v(35.58, 2.53) * mm});
            skLineSegment(sketch, "E334", {"start": v(35.58, 2.53) * mm, "end": v(35.58, 3.53) * mm});
            skLineSegment(sketch, "E335", {"start": v(35.58, 3.53) * mm, "end": v(36.37, 3.53) * mm});
            skLineSegment(sketch, "E336", {"start": v(36.37, 3.53) * mm, "end": v(36.37, 6.63) * mm});
            skLineSegment(sketch, "E337", {"start": v(36.37, 6.63) * mm, "end": v(35.58, 6.63) * mm});
            skLineSegment(sketch, "E338", {"start": v(35.58, 6.63) * mm, "end": v(35.58, 12.43) * mm});
            skLineSegment(sketch, "E339", {"start": v(35.58, 12.43) * mm, "end": v(36.37, 12.43) * mm});
            skLineSegment(sketch, "E340", {"start": v(36.37, 12.43) * mm, "end": v(36.37, 15.53) * mm});
            skLineSegment(sketch, "E341", {"start": v(36.37, 15.53) * mm, "end": v(35.58, 15.53) * mm});
            skLineSegment(sketch, "E342", {"start": v(35.58, 15.53) * mm, "end": v(35.58, 16.53) * mm});
            skLineSegment(sketch, "E343", {"start": v(35.58, 16.53) * mm, "end": v(21.57, 16.53) * mm});
            skLineSegment(sketch, "E344", {"start": v(40.62, 16.53) * mm, "end": v(40.62, 15.53) * mm});
            skLineSegment(sketch, "E345", {"start": v(40.62, 15.53) * mm, "end": v(39.83, 15.53) * mm});
            skLineSegment(sketch, "E346", {"start": v(39.83, 15.53) * mm, "end": v(39.83, 12.43) * mm});
            skLineSegment(sketch, "E347", {"start": v(39.83, 12.43) * mm, "end": v(40.62, 12.43) * mm});
            skLineSegment(sketch, "E348", {"start": v(40.62, 12.43) * mm, "end": v(40.62, 6.63) * mm});
            skLineSegment(sketch, "E349", {"start": v(40.62, 6.63) * mm, "end": v(39.83, 6.63) * mm});
            skLineSegment(sketch, "E350", {"start": v(39.83, 6.63) * mm, "end": v(39.83, 3.53) * mm});
            skLineSegment(sketch, "E351", {"start": v(39.83, 3.53) * mm, "end": v(40.62, 3.53) * mm});
            skLineSegment(sketch, "E352", {"start": v(40.62, 3.53) * mm, "end": v(40.62, 2.53) * mm});
            skLineSegment(sketch, "E353", {"start": v(40.62, 2.53) * mm, "end": v(54.62, 2.53) * mm});
            skLineSegment(sketch, "E354", {"start": v(54.62, 2.53) * mm, "end": v(54.62, 3.53) * mm});
            skLineSegment(sketch, "E355", {"start": v(54.62, 3.53) * mm, "end": v(55.42, 3.53) * mm});
            skLineSegment(sketch, "E356", {"start": v(55.42, 3.53) * mm, "end": v(55.42, 6.63) * mm});
            skLineSegment(sketch, "E357", {"start": v(55.42, 6.63) * mm, "end": v(54.62, 6.63) * mm});
            skLineSegment(sketch, "E358", {"start": v(54.62, 6.63) * mm, "end": v(54.62, 12.43) * mm});
            skLineSegment(sketch, "E359", {"start": v(54.62, 12.43) * mm, "end": v(55.42, 12.43) * mm});
            skLineSegment(sketch, "E360", {"start": v(55.42, 12.43) * mm, "end": v(55.42, 15.53) * mm});
            skLineSegment(sketch, "E361", {"start": v(55.42, 15.53) * mm, "end": v(54.62, 15.53) * mm});
            skLineSegment(sketch, "E362", {"start": v(54.62, 15.53) * mm, "end": v(54.62, 16.53) * mm});
            skLineSegment(sketch, "E363", {"start": v(54.62, 16.53) * mm, "end": v(40.62, 16.53) * mm});
            skLineSegment(sketch, "E364", {"start": v(-54.63, 35.58) * mm, "end": v(-54.63, 34.58) * mm});
            skLineSegment(sketch, "E365", {"start": v(-54.63, 34.58) * mm, "end": v(-55.43, 34.58) * mm});
            skLineSegment(sketch, "E366", {"start": v(-55.43, 34.58) * mm, "end": v(-55.43, 31.48) * mm});
            skLineSegment(sketch, "E367", {"start": v(-55.43, 31.48) * mm, "end": v(-54.63, 31.48) * mm});
            skLineSegment(sketch, "E368", {"start": v(-54.63, 31.48) * mm, "end": v(-54.63, 25.68) * mm});
            skLineSegment(sketch, "E369", {"start": v(-54.63, 25.68) * mm, "end": v(-55.43, 25.68) * mm});
            skLineSegment(sketch, "E370", {"start": v(-55.43, 25.68) * mm, "end": v(-55.43, 22.58) * mm});
            skLineSegment(sketch, "E371", {"start": v(-55.43, 22.58) * mm, "end": v(-54.63, 22.58) * mm});
            skLineSegment(sketch, "E372", {"start": v(-54.63, 22.58) * mm, "end": v(-54.63, 21.58) * mm});
            skLineSegment(sketch, "E373", {"start": v(-54.63, 21.58) * mm, "end": v(-40.62, 21.58) * mm});
            skLineSegment(sketch, "E374", {"start": v(-40.62, 21.58) * mm, "end": v(-40.62, 22.58) * mm});
            skLineSegment(sketch, "E375", {"start": v(-40.62, 22.58) * mm, "end": v(-39.83, 22.58) * mm});
            skLineSegment(sketch, "E376", {"start": v(-39.83, 22.58) * mm, "end": v(-39.83, 25.68) * mm});
            skLineSegment(sketch, "E377", {"start": v(-39.83, 25.68) * mm, "end": v(-40.62, 25.68) * mm});
            skLineSegment(sketch, "E378", {"start": v(-40.62, 25.68) * mm, "end": v(-40.62, 31.48) * mm});
            skLineSegment(sketch, "E379", {"start": v(-40.62, 31.48) * mm, "end": v(-39.83, 31.48) * mm});
            skLineSegment(sketch, "E380", {"start": v(-39.83, 31.48) * mm, "end": v(-39.83, 34.58) * mm});
            skLineSegment(sketch, "E381", {"start": v(-39.83, 34.58) * mm, "end": v(-40.62, 34.58) * mm});
            skLineSegment(sketch, "E382", {"start": v(-40.62, 34.58) * mm, "end": v(-40.62, 35.58) * mm});
            skLineSegment(sketch, "E383", {"start": v(-40.62, 35.58) * mm, "end": v(-54.63, 35.58) * mm});
            skLineSegment(sketch, "E384", {"start": v(-35.58, 35.58) * mm, "end": v(-35.58, 34.58) * mm});
            skLineSegment(sketch, "E385", {"start": v(-35.58, 34.58) * mm, "end": v(-36.37, 34.58) * mm});
            skLineSegment(sketch, "E386", {"start": v(-36.37, 34.58) * mm, "end": v(-36.37, 31.48) * mm});
            skLineSegment(sketch, "E387", {"start": v(-36.37, 31.48) * mm, "end": v(-35.58, 31.48) * mm});
            skLineSegment(sketch, "E388", {"start": v(-35.58, 31.48) * mm, "end": v(-35.58, 25.68) * mm});
            skLineSegment(sketch, "E389", {"start": v(-35.58, 25.68) * mm, "end": v(-36.37, 25.68) * mm});
            skLineSegment(sketch, "E390", {"start": v(-36.37, 25.68) * mm, "end": v(-36.37, 22.58) * mm});
            skLineSegment(sketch, "E391", {"start": v(-36.37, 22.58) * mm, "end": v(-35.58, 22.58) * mm});
            skLineSegment(sketch, "E392", {"start": v(-35.58, 22.58) * mm, "end": v(-35.58, 21.58) * mm});
            skLineSegment(sketch, "E393", {"start": v(-35.58, 21.58) * mm, "end": v(-21.57, 21.58) * mm});
            skLineSegment(sketch, "E394", {"start": v(-21.57, 21.58) * mm, "end": v(-21.57, 22.58) * mm});
            skLineSegment(sketch, "E395", {"start": v(-21.57, 22.58) * mm, "end": v(-20.78, 22.58) * mm});
            skLineSegment(sketch, "E396", {"start": v(-20.78, 22.58) * mm, "end": v(-20.78, 25.68) * mm});
            skLineSegment(sketch, "E397", {"start": v(-20.78, 25.68) * mm, "end": v(-21.57, 25.68) * mm});
            skLineSegment(sketch, "E398", {"start": v(-21.57, 25.68) * mm, "end": v(-21.57, 31.48) * mm});
            skLineSegment(sketch, "E399", {"start": v(-21.57, 31.48) * mm, "end": v(-20.78, 31.48) * mm});
            skLineSegment(sketch, "E400", {"start": v(-20.78, 31.48) * mm, "end": v(-20.78, 34.58) * mm});
            skLineSegment(sketch, "E401", {"start": v(-20.78, 34.58) * mm, "end": v(-21.57, 34.58) * mm});
            skLineSegment(sketch, "E402", {"start": v(-21.57, 34.58) * mm, "end": v(-21.57, 35.58) * mm});
            skLineSegment(sketch, "E403", {"start": v(-21.57, 35.58) * mm, "end": v(-35.58, 35.58) * mm});
            skLineSegment(sketch, "E404", {"start": v(-16.53, 35.58) * mm, "end": v(-16.53, 34.58) * mm});
            skLineSegment(sketch, "E405", {"start": v(-16.53, 34.58) * mm, "end": v(-17.32, 34.58) * mm});
            skLineSegment(sketch, "E406", {"start": v(-17.32, 34.58) * mm, "end": v(-17.32, 31.48) * mm});
            skLineSegment(sketch, "E407", {"start": v(-17.32, 31.48) * mm, "end": v(-16.53, 31.48) * mm});
            skLineSegment(sketch, "E408", {"start": v(-16.53, 31.48) * mm, "end": v(-16.53, 25.68) * mm});
            skLineSegment(sketch, "E409", {"start": v(-16.53, 25.68) * mm, "end": v(-17.32, 25.68) * mm});
            skLineSegment(sketch, "E410", {"start": v(-17.32, 25.68) * mm, "end": v(-17.32, 22.58) * mm});
            skLineSegment(sketch, "E411", {"start": v(-17.32, 22.58) * mm, "end": v(-16.53, 22.58) * mm});
            skLineSegment(sketch, "E412", {"start": v(-16.53, 22.58) * mm, "end": v(-16.53, 21.58) * mm});
            skLineSegment(sketch, "E413", {"start": v(-16.53, 21.58) * mm, "end": v(-2.52, 21.58) * mm});
            skLineSegment(sketch, "E414", {"start": v(-2.52, 21.58) * mm, "end": v(-2.52, 22.58) * mm});
            skLineSegment(sketch, "E415", {"start": v(-2.52, 22.58) * mm, "end": v(-1.73, 22.58) * mm});
            skLineSegment(sketch, "E416", {"start": v(-1.73, 22.58) * mm, "end": v(-1.73, 25.68) * mm});
            skLineSegment(sketch, "E417", {"start": v(-1.73, 25.68) * mm, "end": v(-2.52, 25.68) * mm});
            skLineSegment(sketch, "E418", {"start": v(-2.52, 25.68) * mm, "end": v(-2.52, 31.48) * mm});
            skLineSegment(sketch, "E419", {"start": v(-2.52, 31.48) * mm, "end": v(-1.73, 31.48) * mm});
            skLineSegment(sketch, "E420", {"start": v(-1.73, 31.48) * mm, "end": v(-1.73, 34.58) * mm});
            skLineSegment(sketch, "E421", {"start": v(-1.73, 34.58) * mm, "end": v(-2.52, 34.58) * mm});
            skLineSegment(sketch, "E422", {"start": v(-2.52, 34.58) * mm, "end": v(-2.52, 35.58) * mm});
            skLineSegment(sketch, "E423", {"start": v(-2.52, 35.58) * mm, "end": v(-16.53, 35.58) * mm});
            skLineSegment(sketch, "E424", {"start": v(2.52, 35.58) * mm, "end": v(2.52, 34.58) * mm});
            skLineSegment(sketch, "E425", {"start": v(2.52, 34.58) * mm, "end": v(1.73, 34.58) * mm});
            skLineSegment(sketch, "E426", {"start": v(1.73, 34.58) * mm, "end": v(1.73, 31.48) * mm});
            skLineSegment(sketch, "E427", {"start": v(1.73, 31.48) * mm, "end": v(2.52, 31.48) * mm});
            skLineSegment(sketch, "E428", {"start": v(2.52, 31.48) * mm, "end": v(2.52, 25.68) * mm});
            skLineSegment(sketch, "E429", {"start": v(2.52, 25.68) * mm, "end": v(1.73, 25.68) * mm});
            skLineSegment(sketch, "E430", {"start": v(1.73, 25.68) * mm, "end": v(1.73, 22.58) * mm});
            skLineSegment(sketch, "E431", {"start": v(1.73, 22.58) * mm, "end": v(2.52, 22.58) * mm});
            skLineSegment(sketch, "E432", {"start": v(2.52, 22.58) * mm, "end": v(2.52, 21.58) * mm});
            skLineSegment(sketch, "E433", {"start": v(2.52, 21.58) * mm, "end": v(16.53, 21.58) * mm});
            skLineSegment(sketch, "E434", {"start": v(16.53, 21.58) * mm, "end": v(16.53, 22.58) * mm});
            skLineSegment(sketch, "E435", {"start": v(16.53, 22.58) * mm, "end": v(17.32, 22.58) * mm});
            skLineSegment(sketch, "E436", {"start": v(17.32, 22.58) * mm, "end": v(17.32, 25.68) * mm});
            skLineSegment(sketch, "E437", {"start": v(17.32, 25.68) * mm, "end": v(16.53, 25.68) * mm});
            skLineSegment(sketch, "E438", {"start": v(16.53, 25.68) * mm, "end": v(16.53, 31.48) * mm});
            skLineSegment(sketch, "E439", {"start": v(16.53, 31.48) * mm, "end": v(17.32, 31.48) * mm});
            skLineSegment(sketch, "E440", {"start": v(17.32, 31.48) * mm, "end": v(17.32, 34.58) * mm});
            skLineSegment(sketch, "E441", {"start": v(17.32, 34.58) * mm, "end": v(16.53, 34.58) * mm});
            skLineSegment(sketch, "E442", {"start": v(16.53, 34.58) * mm, "end": v(16.53, 35.58) * mm});
            skLineSegment(sketch, "E443", {"start": v(16.53, 35.58) * mm, "end": v(2.52, 35.58) * mm});
            skLineSegment(sketch, "E444", {"start": v(21.57, 35.58) * mm, "end": v(21.57, 34.58) * mm});
            skLineSegment(sketch, "E445", {"start": v(21.57, 34.58) * mm, "end": v(20.78, 34.58) * mm});
            skLineSegment(sketch, "E446", {"start": v(20.78, 34.58) * mm, "end": v(20.78, 31.48) * mm});
            skLineSegment(sketch, "E447", {"start": v(20.78, 31.48) * mm, "end": v(21.57, 31.48) * mm});
            skLineSegment(sketch, "E448", {"start": v(21.57, 31.48) * mm, "end": v(21.57, 25.68) * mm});
            skLineSegment(sketch, "E449", {"start": v(21.57, 25.68) * mm, "end": v(20.78, 25.68) * mm});
            skLineSegment(sketch, "E450", {"start": v(20.78, 25.68) * mm, "end": v(20.78, 22.58) * mm});
            skLineSegment(sketch, "E451", {"start": v(20.78, 22.58) * mm, "end": v(21.57, 22.58) * mm});
            skLineSegment(sketch, "E452", {"start": v(21.57, 22.58) * mm, "end": v(21.57, 21.58) * mm});
            skLineSegment(sketch, "E453", {"start": v(21.57, 21.58) * mm, "end": v(35.58, 21.58) * mm});
            skLineSegment(sketch, "E454", {"start": v(35.58, 21.58) * mm, "end": v(35.58, 22.58) * mm});
            skLineSegment(sketch, "E455", {"start": v(35.58, 22.58) * mm, "end": v(36.37, 22.58) * mm});
            skLineSegment(sketch, "E456", {"start": v(36.37, 22.58) * mm, "end": v(36.37, 25.68) * mm});
            skLineSegment(sketch, "E457", {"start": v(36.37, 25.68) * mm, "end": v(35.58, 25.68) * mm});
            skLineSegment(sketch, "E458", {"start": v(35.58, 25.68) * mm, "end": v(35.58, 31.48) * mm});
            skLineSegment(sketch, "E459", {"start": v(35.58, 31.48) * mm, "end": v(36.37, 31.48) * mm});
            skLineSegment(sketch, "E460", {"start": v(36.37, 31.48) * mm, "end": v(36.37, 34.58) * mm});
            skLineSegment(sketch, "E461", {"start": v(36.37, 34.58) * mm, "end": v(35.58, 34.58) * mm});
            skLineSegment(sketch, "E462", {"start": v(35.58, 34.58) * mm, "end": v(35.58, 35.58) * mm});
            skLineSegment(sketch, "E463", {"start": v(35.58, 35.58) * mm, "end": v(21.57, 35.58) * mm});
            skLineSegment(sketch, "E464", {"start": v(40.62, 35.58) * mm, "end": v(40.62, 34.58) * mm});
            skLineSegment(sketch, "E465", {"start": v(40.62, 34.58) * mm, "end": v(39.83, 34.58) * mm});
            skLineSegment(sketch, "E466", {"start": v(39.83, 34.58) * mm, "end": v(39.83, 31.48) * mm});
            skLineSegment(sketch, "E467", {"start": v(39.83, 31.48) * mm, "end": v(40.62, 31.48) * mm});
            skLineSegment(sketch, "E468", {"start": v(40.62, 31.48) * mm, "end": v(40.62, 25.68) * mm});
            skLineSegment(sketch, "E469", {"start": v(40.62, 25.68) * mm, "end": v(39.83, 25.68) * mm});
            skLineSegment(sketch, "E470", {"start": v(39.83, 25.68) * mm, "end": v(39.83, 22.58) * mm});
            skLineSegment(sketch, "E471", {"start": v(39.83, 22.58) * mm, "end": v(40.62, 22.58) * mm});
            skLineSegment(sketch, "E472", {"start": v(40.62, 22.58) * mm, "end": v(40.62, 21.58) * mm});
            skLineSegment(sketch, "E473", {"start": v(40.62, 21.58) * mm, "end": v(54.62, 21.58) * mm});
            skLineSegment(sketch, "E474", {"start": v(54.62, 21.58) * mm, "end": v(54.62, 22.58) * mm});
            skLineSegment(sketch, "E475", {"start": v(54.62, 22.58) * mm, "end": v(55.42, 22.58) * mm});
            skLineSegment(sketch, "E476", {"start": v(55.42, 22.58) * mm, "end": v(55.42, 25.68) * mm});
            skLineSegment(sketch, "E477", {"start": v(55.42, 25.68) * mm, "end": v(54.62, 25.68) * mm});
            skLineSegment(sketch, "E478", {"start": v(54.62, 25.68) * mm, "end": v(54.62, 31.48) * mm});
            skLineSegment(sketch, "E479", {"start": v(54.62, 31.48) * mm, "end": v(55.42, 31.48) * mm});
            skLineSegment(sketch, "E480", {"start": v(55.42, 31.48) * mm, "end": v(55.42, 34.58) * mm});
            skLineSegment(sketch, "E481", {"start": v(55.42, 34.58) * mm, "end": v(54.62, 34.58) * mm});
            skLineSegment(sketch, "E482", {"start": v(54.62, 34.58) * mm, "end": v(54.62, 35.58) * mm});
            skLineSegment(sketch, "E483", {"start": v(54.62, 35.58) * mm, "end": v(40.62, 35.58) * mm});
            skLineSegment(sketch, "E484.bottom", {"start": v(67.5, 49) * mm, "end": v(-67.5, 49) * mm});
            skLineSegment(sketch, "E484.top", {"start": v(67.5, -49) * mm, "end": v(-67.5, -49) * mm});
            skLineSegment(sketch, "E484.left", {"start": v(67.5, 49) * mm, "end": v(67.5, -49) * mm});
            skLineSegment(sketch, "E484.right", {"start": v(-67.5, 49) * mm, "end": v(-67.5, -49) * mm});
            skPoint(sketch, "E484.middle", {"position": v(0, 0) * mm});
            skSolve(sketch);
        }
        {
            var Q0;
            Q0=makeQuery(id+"F0.imprint","IMPRINT",FACE,{"disambiguationData":[TD([[makeQuery(id+"F0.imprint","IMPRINT",EDGE,{"derivedFrom":sQuery(id+"F0.wireOp",EDGE,"E0")}),1.0]])]});
            var Q1;
            Q1=makeQuery(id+"F0.imprint","IMPRINT",FACE,{"disambiguationData":[TD([[makeQuery(id+"F0.imprint","IMPRINT",EDGE,{"derivedFrom":sQuery(id+"F0.wireOp",EDGE,"E0")}),-1.0]])]});
            extrude(context, id + "F1", {"entities" : qUnion([Q0, Q1]), "depth" : 1.4 * mm, "offsetDistance" : 25 * mm});
        }
        {
            var Q0;
            Q0=makeQuery(id+"F1.opExtrude","CAP_FACE",FACE,{"disambiguationData":[OSD([sQuery(id+"F0.wireOp",EDGE,"E4"),sQuery(id+"F0.wireOp",EDGE,"E5"),sQuery(id+"F0.wireOp",EDGE,"E6"),sQuery(id+"F0.wireOp",EDGE,"E7"),sQuery(id+"F0.wireOp",EDGE,"E8"),sQuery(id+"F0.wireOp",EDGE,"E9"),sQuery(id+"F0.wireOp",EDGE,"E10"),sQuery(id+"F0.wireOp",EDGE,"E11"),sQuery(id+"F0.wireOp",EDGE,"E12"),sQuery(id+"F0.wireOp",EDGE,"E13"),sQuery(id+"F0.wireOp",EDGE,"E14"),sQuery(id+"F0.wireOp",EDGE,"E15"),sQuery(id+"F0.wireOp",EDGE,"E16"),sQuery(id+"F0.wireOp",EDGE,"E17"),sQuery(id+"F0.wireOp",EDGE,"E18"),sQuery(id+"F0.wireOp",EDGE,"E19"),sQuery(id+"F0.wireOp",EDGE,"E20"),sQuery(id+"F0.wireOp",EDGE,"E21"),sQuery(id+"F0.wireOp",EDGE,"E22"),sQuery(id+"F0.wireOp",EDGE,"E23"),sQuery(id+"F0.wireOp",EDGE,"E24"),sQuery(id+"F0.wireOp",EDGE,"E25"),sQuery(id+"F0.wireOp",EDGE,"E26"),sQuery(id+"F0.wireOp",EDGE,"E27"),sQuery(id+"F0.wireOp",EDGE,"E28"),sQuery(id+"F0.wireOp",EDGE,"E29"),sQuery(id+"F0.wireOp",EDGE,"E30"),sQuery(id+"F0.wireOp",EDGE,"E31"),sQuery(id+"F0.wireOp",EDGE,"E32"),sQuery(id+"F0.wireOp",EDGE,"E33"),sQuery(id+"F0.wireOp",EDGE,"E34"),sQuery(id+"F0.wireOp",EDGE,"E35"),sQuery(id+"F0.wireOp",EDGE,"E36"),sQuery(id+"F0.wireOp",EDGE,"E37"),sQuery(id+"F0.wireOp",EDGE,"E38"),sQuery(id+"F0.wireOp",EDGE,"E39"),sQuery(id+"F0.wireOp",EDGE,"E40"),sQuery(id+"F0.wireOp",EDGE,"E41"),sQuery(id+"F0.wireOp",EDGE,"E42"),sQuery(id+"F0.wireOp",EDGE,"E43"),sQuery(id+"F0.wireOp",EDGE,"E44"),sQuery(id+"F0.wireOp",EDGE,"E45"),sQuery(id+"F0.wireOp",EDGE,"E46"),sQuery(id+"F0.wireOp",EDGE,"E47"),sQuery(id+"F0.wireOp",EDGE,"E48"),sQuery(id+"F0.wireOp",EDGE,"E49"),sQuery(id+"F0.wireOp",EDGE,"E50"),sQuery(id+"F0.wireOp",EDGE,"E51"),sQuery(id+"F0.wireOp",EDGE,"E52"),sQuery(id+"F0.wireOp",EDGE,"E53"),sQuery(id+"F0.wireOp",EDGE,"E54"),sQuery(id+"F0.wireOp",EDGE,"E55"),sQuery(id+"F0.wireOp",EDGE,"E56"),sQuery(id+"F0.wireOp",EDGE,"E57"),sQuery(id+"F0.wireOp",EDGE,"E58"),sQuery(id+"F0.wireOp",EDGE,"E59"),sQuery(id+"F0.wireOp",EDGE,"E60"),sQuery(id+"F0.wireOp",EDGE,"E61"),sQuery(id+"F0.wireOp",EDGE,"E62"),sQuery(id+"F0.wireOp",EDGE,"E63"),sQuery(id+"F0.wireOp",EDGE,"E64"),sQuery(id+"F0.wireOp",EDGE,"E65"),sQuery(id+"F0.wireOp",EDGE,"E66"),sQuery(id+"F0.wireOp",EDGE,"E67"),sQuery(id+"F0.wireOp",EDGE,"E68"),sQuery(id+"F0.wireOp",EDGE,"E69"),sQuery(id+"F0.wireOp",EDGE,"E70"),sQuery(id+"F0.wireOp",EDGE,"E71"),sQuery(id+"F0.wireOp",EDGE,"E72"),sQuery(id+"F0.wireOp",EDGE,"E73"),sQuery(id+"F0.wireOp",EDGE,"E74"),sQuery(id+"F0.wireOp",EDGE,"E75"),sQuery(id+"F0.wireOp",EDGE,"E76"),sQuery(id+"F0.wireOp",EDGE,"E77"),sQuery(id+"F0.wireOp",EDGE,"E78"),sQuery(id+"F0.wireOp",EDGE,"E79"),sQuery(id+"F0.wireOp",EDGE,"E80"),sQuery(id+"F0.wireOp",EDGE,"E81"),sQuery(id+"F0.wireOp",EDGE,"E82"),sQuery(id+"F0.wireOp",EDGE,"E83"),sQuery(id+"F0.wireOp",EDGE,"E84"),sQuery(id+"F0.wireOp",EDGE,"E85"),sQuery(id+"F0.wireOp",EDGE,"E86"),sQuery(id+"F0.wireOp",EDGE,"E87"),sQuery(id+"F0.wireOp",EDGE,"E88"),sQuery(id+"F0.wireOp",EDGE,"E89"),sQuery(id+"F0.wireOp",EDGE,"E90"),sQuery(id+"F0.wireOp",EDGE,"E91"),sQuery(id+"F0.wireOp",EDGE,"E92"),sQuery(id+"F0.wireOp",EDGE,"E93"),sQuery(id+"F0.wireOp",EDGE,"E94"),sQuery(id+"F0.wireOp",EDGE,"E95"),sQuery(id+"F0.wireOp",EDGE,"E96"),sQuery(id+"F0.wireOp",EDGE,"E97"),sQuery(id+"F0.wireOp",EDGE,"E98"),sQuery(id+"F0.wireOp",EDGE,"E99"),sQuery(id+"F0.wireOp",EDGE,"E100"),sQuery(id+"F0.wireOp",EDGE,"E101"),sQuery(id+"F0.wireOp",EDGE,"E102"),sQuery(id+"F0.wireOp",EDGE,"E103"),sQuery(id+"F0.wireOp",EDGE,"E104"),sQuery(id+"F0.wireOp",EDGE,"E105"),sQuery(id+"F0.wireOp",EDGE,"E106"),sQuery(id+"F0.wireOp",EDGE,"E107"),sQuery(id+"F0.wireOp",EDGE,"E108"),sQuery(id+"F0.wireOp",EDGE,"E109"),sQuery(id+"F0.wireOp",EDGE,"E110"),sQuery(id+"F0.wireOp",EDGE,"E111"),sQuery(id+"F0.wireOp",EDGE,"E112"),sQuery(id+"F0.wireOp",EDGE,"E113"),sQuery(id+"F0.wireOp",EDGE,"E114"),sQuery(id+"F0.wireOp",EDGE,"E115"),sQuery(id+"F0.wireOp",EDGE,"E116"),sQuery(id+"F0.wireOp",EDGE,"E117"),sQuery(id+"F0.wireOp",EDGE,"E118"),sQuery(id+"F0.wireOp",EDGE,"E119"),sQuery(id+"F0.wireOp",EDGE,"E120"),sQuery(id+"F0.wireOp",EDGE,"E121"),sQuery(id+"F0.wireOp",EDGE,"E122"),sQuery(id+"F0.wireOp",EDGE,"E123"),sQuery(id+"F0.wireOp",EDGE,"E124"),sQuery(id+"F0.wireOp",EDGE,"E125"),sQuery(id+"F0.wireOp",EDGE,"E126"),sQuery(id+"F0.wireOp",EDGE,"E127"),sQuery(id+"F0.wireOp",EDGE,"E128"),sQuery(id+"F0.wireOp",EDGE,"E129"),sQuery(id+"F0.wireOp",EDGE,"E130"),sQuery(id+"F0.wireOp",EDGE,"E131"),sQuery(id+"F0.wireOp",EDGE,"E132"),sQuery(id+"F0.wireOp",EDGE,"E133"),sQuery(id+"F0.wireOp",EDGE,"E134"),sQuery(id+"F0.wireOp",EDGE,"E135"),sQuery(id+"F0.wireOp",EDGE,"E136"),sQuery(id+"F0.wireOp",EDGE,"E137"),sQuery(id+"F0.wireOp",EDGE,"E138"),sQuery(id+"F0.wireOp",EDGE,"E139"),sQuery(id+"F0.wireOp",EDGE,"E140"),sQuery(id+"F0.wireOp",EDGE,"E141"),sQuery(id+"F0.wireOp",EDGE,"E142"),sQuery(id+"F0.wireOp",EDGE,"E143"),sQuery(id+"F0.wireOp",EDGE,"E144"),sQuery(id+"F0.wireOp",EDGE,"E145"),sQuery(id+"F0.wireOp",EDGE,"E146"),sQuery(id+"F0.wireOp",EDGE,"E147"),sQuery(id+"F0.wireOp",EDGE,"E148"),sQuery(id+"F0.wireOp",EDGE,"E149"),sQuery(id+"F0.wireOp",EDGE,"E150"),sQuery(id+"F0.wireOp",EDGE,"E151"),sQuery(id+"F0.wireOp",EDGE,"E152"),sQuery(id+"F0.wireOp",EDGE,"E153"),sQuery(id+"F0.wireOp",EDGE,"E154"),sQuery(id+"F0.wireOp",EDGE,"E155"),sQuery(id+"F0.wireOp",EDGE,"E156"),sQuery(id+"F0.wireOp",EDGE,"E157"),sQuery(id+"F0.wireOp",EDGE,"E158"),sQuery(id+"F0.wireOp",EDGE,"E159"),sQuery(id+"F0.wireOp",EDGE,"E160"),sQuery(id+"F0.wireOp",EDGE,"E161"),sQuery(id+"F0.wireOp",EDGE,"E162"),sQuery(id+"F0.wireOp",EDGE,"E163"),sQuery(id+"F0.wireOp",EDGE,"E164"),sQuery(id+"F0.wireOp",EDGE,"E165"),sQuery(id+"F0.wireOp",EDGE,"E166"),sQuery(id+"F0.wireOp",EDGE,"E167"),sQuery(id+"F0.wireOp",EDGE,"E168"),sQuery(id+"F0.wireOp",EDGE,"E169"),sQuery(id+"F0.wireOp",EDGE,"E170"),sQuery(id+"F0.wireOp",EDGE,"E171"),sQuery(id+"F0.wireOp",EDGE,"E172"),sQuery(id+"F0.wireOp",EDGE,"E173"),sQuery(id+"F0.wireOp",EDGE,"E174"),sQuery(id+"F0.wireOp",EDGE,"E175"),sQuery(id+"F0.wireOp",EDGE,"E176"),sQuery(id+"F0.wireOp",EDGE,"E177"),sQuery(id+"F0.wireOp",EDGE,"E178"),sQuery(id+"F0.wireOp",EDGE,"E179"),sQuery(id+"F0.wireOp",EDGE,"E180"),sQuery(id+"F0.wireOp",EDGE,"E181"),sQuery(id+"F0.wireOp",EDGE,"E182"),sQuery(id+"F0.wireOp",EDGE,"E183"),sQuery(id+"F0.wireOp",EDGE,"E184"),sQuery(id+"F0.wireOp",EDGE,"E185"),sQuery(id+"F0.wireOp",EDGE,"E186"),sQuery(id+"F0.wireOp",EDGE,"E187"),sQuery(id+"F0.wireOp",EDGE,"E188"),sQuery(id+"F0.wireOp",EDGE,"E189"),sQuery(id+"F0.wireOp",EDGE,"E190"),sQuery(id+"F0.wireOp",EDGE,"E191"),sQuery(id+"F0.wireOp",EDGE,"E192"),sQuery(id+"F0.wireOp",EDGE,"E193"),sQuery(id+"F0.wireOp",EDGE,"E194"),sQuery(id+"F0.wireOp",EDGE,"E195"),sQuery(id+"F0.wireOp",EDGE,"E196"),sQuery(id+"F0.wireOp",EDGE,"E197"),sQuery(id+"F0.wireOp",EDGE,"E198"),sQuery(id+"F0.wireOp",EDGE,"E199"),sQuery(id+"F0.wireOp",EDGE,"E200"),sQuery(id+"F0.wireOp",EDGE,"E201"),sQuery(id+"F0.wireOp",EDGE,"E202"),sQuery(id+"F0.wireOp",EDGE,"E203"),sQuery(id+"F0.wireOp",EDGE,"E204"),sQuery(id+"F0.wireOp",EDGE,"E205"),sQuery(id+"F0.wireOp",EDGE,"E206"),sQuery(id+"F0.wireOp",EDGE,"E207"),sQuery(id+"F0.wireOp",EDGE,"E208"),sQuery(id+"F0.wireOp",EDGE,"E209"),sQuery(id+"F0.wireOp",EDGE,"E210"),sQuery(id+"F0.wireOp",EDGE,"E211"),sQuery(id+"F0.wireOp",EDGE,"E212"),sQuery(id+"F0.wireOp",EDGE,"E213"),sQuery(id+"F0.wireOp",EDGE,"E214"),sQuery(id+"F0.wireOp",EDGE,"E215"),sQuery(id+"F0.wireOp",EDGE,"E216"),sQuery(id+"F0.wireOp",EDGE,"E217"),sQuery(id+"F0.wireOp",EDGE,"E218"),sQuery(id+"F0.wireOp",EDGE,"E219"),sQuery(id+"F0.wireOp",EDGE,"E220"),sQuery(id+"F0.wireOp",EDGE,"E221"),sQuery(id+"F0.wireOp",EDGE,"E222"),sQuery(id+"F0.wireOp",EDGE,"E223"),sQuery(id+"F0.wireOp",EDGE,"E224"),sQuery(id+"F0.wireOp",EDGE,"E225"),sQuery(id+"F0.wireOp",EDGE,"E226"),sQuery(id+"F0.wireOp",EDGE,"E227"),sQuery(id+"F0.wireOp",EDGE,"E228"),sQuery(id+"F0.wireOp",EDGE,"E229"),sQuery(id+"F0.wireOp",EDGE,"E230"),sQuery(id+"F0.wireOp",EDGE,"E231"),sQuery(id+"F0.wireOp",EDGE,"E232"),sQuery(id+"F0.wireOp",EDGE,"E233"),sQuery(id+"F0.wireOp",EDGE,"E234"),sQuery(id+"F0.wireOp",EDGE,"E235"),sQuery(id+"F0.wireOp",EDGE,"E236"),sQuery(id+"F0.wireOp",EDGE,"E237"),sQuery(id+"F0.wireOp",EDGE,"E238"),sQuery(id+"F0.wireOp",EDGE,"E239"),sQuery(id+"F0.wireOp",EDGE,"E240"),sQuery(id+"F0.wireOp",EDGE,"E241"),sQuery(id+"F0.wireOp",EDGE,"E242"),sQuery(id+"F0.wireOp",EDGE,"E243"),sQuery(id+"F0.wireOp",EDGE,"E244"),sQuery(id+"F0.wireOp",EDGE,"E245"),sQuery(id+"F0.wireOp",EDGE,"E246"),sQuery(id+"F0.wireOp",EDGE,"E247"),sQuery(id+"F0.wireOp",EDGE,"E248"),sQuery(id+"F0.wireOp",EDGE,"E249"),sQuery(id+"F0.wireOp",EDGE,"E250"),sQuery(id+"F0.wireOp",EDGE,"E251"),sQuery(id+"F0.wireOp",EDGE,"E252"),sQuery(id+"F0.wireOp",EDGE,"E253"),sQuery(id+"F0.wireOp",EDGE,"E254"),sQuery(id+"F0.wireOp",EDGE,"E255"),sQuery(id+"F0.wireOp",EDGE,"E256"),sQuery(id+"F0.wireOp",EDGE,"E257"),sQuery(id+"F0.wireOp",EDGE,"E258"),sQuery(id+"F0.wireOp",EDGE,"E259"),sQuery(id+"F0.wireOp",EDGE,"E260"),sQuery(id+"F0.wireOp",EDGE,"E261"),sQuery(id+"F0.wireOp",EDGE,"E262"),sQuery(id+"F0.wireOp",EDGE,"E263"),sQuery(id+"F0.wireOp",EDGE,"E264"),sQuery(id+"F0.wireOp",EDGE,"E265"),sQuery(id+"F0.wireOp",EDGE,"E266"),sQuery(id+"F0.wireOp",EDGE,"E267"),sQuery(id+"F0.wireOp",EDGE,"E268"),sQuery(id+"F0.wireOp",EDGE,"E269"),sQuery(id+"F0.wireOp",EDGE,"E270"),sQuery(id+"F0.wireOp",EDGE,"E271"),sQuery(id+"F0.wireOp",EDGE,"E272"),sQuery(id+"F0.wireOp",EDGE,"E273"),sQuery(id+"F0.wireOp",EDGE,"E274"),sQuery(id+"F0.wireOp",EDGE,"E275"),sQuery(id+"F0.wireOp",EDGE,"E276"),sQuery(id+"F0.wireOp",EDGE,"E277"),sQuery(id+"F0.wireOp",EDGE,"E278"),sQuery(id+"F0.wireOp",EDGE,"E279"),sQuery(id+"F0.wireOp",EDGE,"E280"),sQuery(id+"F0.wireOp",EDGE,"E281"),sQuery(id+"F0.wireOp",EDGE,"E282"),sQuery(id+"F0.wireOp",EDGE,"E283"),sQuery(id+"F0.wireOp",EDGE,"E284"),sQuery(id+"F0.wireOp",EDGE,"E285"),sQuery(id+"F0.wireOp",EDGE,"E286"),sQuery(id+"F0.wireOp",EDGE,"E287"),sQuery(id+"F0.wireOp",EDGE,"E288"),sQuery(id+"F0.wireOp",EDGE,"E289"),sQuery(id+"F0.wireOp",EDGE,"E290"),sQuery(id+"F0.wireOp",EDGE,"E291"),sQuery(id+"F0.wireOp",EDGE,"E292"),sQuery(id+"F0.wireOp",EDGE,"E293"),sQuery(id+"F0.wireOp",EDGE,"E294"),sQuery(id+"F0.wireOp",EDGE,"E295"),sQuery(id+"F0.wireOp",EDGE,"E296"),sQuery(id+"F0.wireOp",EDGE,"E297"),sQuery(id+"F0.wireOp",EDGE,"E298"),sQuery(id+"F0.wireOp",EDGE,"E299"),sQuery(id+"F0.wireOp",EDGE,"E300"),sQuery(id+"F0.wireOp",EDGE,"E301"),sQuery(id+"F0.wireOp",EDGE,"E302"),sQuery(id+"F0.wireOp",EDGE,"E303"),sQuery(id+"F0.wireOp",EDGE,"E304"),sQuery(id+"F0.wireOp",EDGE,"E305"),sQuery(id+"F0.wireOp",EDGE,"E306"),sQuery(id+"F0.wireOp",EDGE,"E307"),sQuery(id+"F0.wireOp",EDGE,"E308"),sQuery(id+"F0.wireOp",EDGE,"E309"),sQuery(id+"F0.wireOp",EDGE,"E310"),sQuery(id+"F0.wireOp",EDGE,"E311"),sQuery(id+"F0.wireOp",EDGE,"E312"),sQuery(id+"F0.wireOp",EDGE,"E313"),sQuery(id+"F0.wireOp",EDGE,"E314"),sQuery(id+"F0.wireOp",EDGE,"E315"),sQuery(id+"F0.wireOp",EDGE,"E316"),sQuery(id+"F0.wireOp",EDGE,"E317"),sQuery(id+"F0.wireOp",EDGE,"E318"),sQuery(id+"F0.wireOp",EDGE,"E319"),sQuery(id+"F0.wireOp",EDGE,"E320"),sQuery(id+"F0.wireOp",EDGE,"E321"),sQuery(id+"F0.wireOp",EDGE,"E322"),sQuery(id+"F0.wireOp",EDGE,"E323"),sQuery(id+"F0.wireOp",EDGE,"E324"),sQuery(id+"F0.wireOp",EDGE,"E325"),sQuery(id+"F0.wireOp",EDGE,"E326"),sQuery(id+"F0.wireOp",EDGE,"E327"),sQuery(id+"F0.wireOp",EDGE,"E328"),sQuery(id+"F0.wireOp",EDGE,"E329"),sQuery(id+"F0.wireOp",EDGE,"E330"),sQuery(id+"F0.wireOp",EDGE,"E331"),sQuery(id+"F0.wireOp",EDGE,"E332"),sQuery(id+"F0.wireOp",EDGE,"E333"),sQuery(id+"F0.wireOp",EDGE,"E334"),sQuery(id+"F0.wireOp",EDGE,"E335"),sQuery(id+"F0.wireOp",EDGE,"E336"),sQuery(id+"F0.wireOp",EDGE,"E337"),sQuery(id+"F0.wireOp",EDGE,"E338"),sQuery(id+"F0.wireOp",EDGE,"E339"),sQuery(id+"F0.wireOp",EDGE,"E340"),sQuery(id+"F0.wireOp",EDGE,"E341"),sQuery(id+"F0.wireOp",EDGE,"E342"),sQuery(id+"F0.wireOp",EDGE,"E343"),sQuery(id+"F0.wireOp",EDGE,"E344"),sQuery(id+"F0.wireOp",EDGE,"E345"),sQuery(id+"F0.wireOp",EDGE,"E346"),sQuery(id+"F0.wireOp",EDGE,"E347"),sQuery(id+"F0.wireOp",EDGE,"E348"),sQuery(id+"F0.wireOp",EDGE,"E349"),sQuery(id+"F0.wireOp",EDGE,"E350"),sQuery(id+"F0.wireOp",EDGE,"E351"),sQuery(id+"F0.wireOp",EDGE,"E352"),sQuery(id+"F0.wireOp",EDGE,"E353"),sQuery(id+"F0.wireOp",EDGE,"E354"),sQuery(id+"F0.wireOp",EDGE,"E355"),sQuery(id+"F0.wireOp",EDGE,"E356"),sQuery(id+"F0.wireOp",EDGE,"E357"),sQuery(id+"F0.wireOp",EDGE,"E358"),sQuery(id+"F0.wireOp",EDGE,"E359"),sQuery(id+"F0.wireOp",EDGE,"E360"),sQuery(id+"F0.wireOp",EDGE,"E361"),sQuery(id+"F0.wireOp",EDGE,"E362"),sQuery(id+"F0.wireOp",EDGE,"E363"),sQuery(id+"F0.wireOp",EDGE,"E364"),sQuery(id+"F0.wireOp",EDGE,"E365"),sQuery(id+"F0.wireOp",EDGE,"E366"),sQuery(id+"F0.wireOp",EDGE,"E367"),sQuery(id+"F0.wireOp",EDGE,"E368"),sQuery(id+"F0.wireOp",EDGE,"E369"),sQuery(id+"F0.wireOp",EDGE,"E370"),sQuery(id+"F0.wireOp",EDGE,"E371"),sQuery(id+"F0.wireOp",EDGE,"E372"),sQuery(id+"F0.wireOp",EDGE,"E373"),sQuery(id+"F0.wireOp",EDGE,"E374"),sQuery(id+"F0.wireOp",EDGE,"E375"),sQuery(id+"F0.wireOp",EDGE,"E376"),sQuery(id+"F0.wireOp",EDGE,"E377"),sQuery(id+"F0.wireOp",EDGE,"E378"),sQuery(id+"F0.wireOp",EDGE,"E379"),sQuery(id+"F0.wireOp",EDGE,"E380"),sQuery(id+"F0.wireOp",EDGE,"E381"),sQuery(id+"F0.wireOp",EDGE,"E382"),sQuery(id+"F0.wireOp",EDGE,"E383"),sQuery(id+"F0.wireOp",EDGE,"E384"),sQuery(id+"F0.wireOp",EDGE,"E385"),sQuery(id+"F0.wireOp",EDGE,"E386"),sQuery(id+"F0.wireOp",EDGE,"E387"),sQuery(id+"F0.wireOp",EDGE,"E388"),sQuery(id+"F0.wireOp",EDGE,"E389"),sQuery(id+"F0.wireOp",EDGE,"E390"),sQuery(id+"F0.wireOp",EDGE,"E391"),sQuery(id+"F0.wireOp",EDGE,"E392"),sQuery(id+"F0.wireOp",EDGE,"E393"),sQuery(id+"F0.wireOp",EDGE,"E394"),sQuery(id+"F0.wireOp",EDGE,"E395"),sQuery(id+"F0.wireOp",EDGE,"E396"),sQuery(id+"F0.wireOp",EDGE,"E397"),sQuery(id+"F0.wireOp",EDGE,"E398"),sQuery(id+"F0.wireOp",EDGE,"E399"),sQuery(id+"F0.wireOp",EDGE,"E400"),sQuery(id+"F0.wireOp",EDGE,"E401"),sQuery(id+"F0.wireOp",EDGE,"E402"),sQuery(id+"F0.wireOp",EDGE,"E403"),sQuery(id+"F0.wireOp",EDGE,"E404"),sQuery(id+"F0.wireOp",EDGE,"E405"),sQuery(id+"F0.wireOp",EDGE,"E406"),sQuery(id+"F0.wireOp",EDGE,"E407"),sQuery(id+"F0.wireOp",EDGE,"E408"),sQuery(id+"F0.wireOp",EDGE,"E409"),sQuery(id+"F0.wireOp",EDGE,"E410"),sQuery(id+"F0.wireOp",EDGE,"E411"),sQuery(id+"F0.wireOp",EDGE,"E412"),sQuery(id+"F0.wireOp",EDGE,"E413"),sQuery(id+"F0.wireOp",EDGE,"E414"),sQuery(id+"F0.wireOp",EDGE,"E415"),sQuery(id+"F0.wireOp",EDGE,"E416"),sQuery(id+"F0.wireOp",EDGE,"E417"),sQuery(id+"F0.wireOp",EDGE,"E418"),sQuery(id+"F0.wireOp",EDGE,"E419"),sQuery(id+"F0.wireOp",EDGE,"E420"),sQuery(id+"F0.wireOp",EDGE,"E421"),sQuery(id+"F0.wireOp",EDGE,"E422"),sQuery(id+"F0.wireOp",EDGE,"E423"),sQuery(id+"F0.wireOp",EDGE,"E424"),sQuery(id+"F0.wireOp",EDGE,"E425"),sQuery(id+"F0.wireOp",EDGE,"E426"),sQuery(id+"F0.wireOp",EDGE,"E427"),sQuery(id+"F0.wireOp",EDGE,"E428"),sQuery(id+"F0.wireOp",EDGE,"E429"),sQuery(id+"F0.wireOp",EDGE,"E430"),sQuery(id+"F0.wireOp",EDGE,"E431"),sQuery(id+"F0.wireOp",EDGE,"E432"),sQuery(id+"F0.wireOp",EDGE,"E433"),sQuery(id+"F0.wireOp",EDGE,"E434"),sQuery(id+"F0.wireOp",EDGE,"E435"),sQuery(id+"F0.wireOp",EDGE,"E436"),sQuery(id+"F0.wireOp",EDGE,"E437"),sQuery(id+"F0.wireOp",EDGE,"E438"),sQuery(id+"F0.wireOp",EDGE,"E439"),sQuery(id+"F0.wireOp",EDGE,"E440"),sQuery(id+"F0.wireOp",EDGE,"E441"),sQuery(id+"F0.wireOp",EDGE,"E442"),sQuery(id+"F0.wireOp",EDGE,"E443"),sQuery(id+"F0.wireOp",EDGE,"E444"),sQuery(id+"F0.wireOp",EDGE,"E445"),sQuery(id+"F0.wireOp",EDGE,"E446"),sQuery(id+"F0.wireOp",EDGE,"E447"),sQuery(id+"F0.wireOp",EDGE,"E448"),sQuery(id+"F0.wireOp",EDGE,"E449"),sQuery(id+"F0.wireOp",EDGE,"E450"),sQuery(id+"F0.wireOp",EDGE,"E451"),sQuery(id+"F0.wireOp",EDGE,"E452"),sQuery(id+"F0.wireOp",EDGE,"E453"),sQuery(id+"F0.wireOp",EDGE,"E454"),sQuery(id+"F0.wireOp",EDGE,"E455"),sQuery(id+"F0.wireOp",EDGE,"E456"),sQuery(id+"F0.wireOp",EDGE,"E457"),sQuery(id+"F0.wireOp",EDGE,"E458"),sQuery(id+"F0.wireOp",EDGE,"E459"),sQuery(id+"F0.wireOp",EDGE,"E460"),sQuery(id+"F0.wireOp",EDGE,"E461"),sQuery(id+"F0.wireOp",EDGE,"E462"),sQuery(id+"F0.wireOp",EDGE,"E463"),sQuery(id+"F0.wireOp",EDGE,"E464"),sQuery(id+"F0.wireOp",EDGE,"E465"),sQuery(id+"F0.wireOp",EDGE,"E466"),sQuery(id+"F0.wireOp",EDGE,"E467"),sQuery(id+"F0.wireOp",EDGE,"E468"),sQuery(id+"F0.wireOp",EDGE,"E469"),sQuery(id+"F0.wireOp",EDGE,"E470"),sQuery(id+"F0.wireOp",EDGE,"E471"),sQuery(id+"F0.wireOp",EDGE,"E472"),sQuery(id+"F0.wireOp",EDGE,"E473"),sQuery(id+"F0.wireOp",EDGE,"E474"),sQuery(id+"F0.wireOp",EDGE,"E475"),sQuery(id+"F0.wireOp",EDGE,"E476"),sQuery(id+"F0.wireOp",EDGE,"E477"),sQuery(id+"F0.wireOp",EDGE,"E478"),sQuery(id+"F0.wireOp",EDGE,"E479"),sQuery(id+"F0.wireOp",EDGE,"E480"),sQuery(id+"F0.wireOp",EDGE,"E481"),sQuery(id+"F0.wireOp",EDGE,"E482"),sQuery(id+"F0.wireOp",EDGE,"E483"),sQuery(id+"F0.wireOp",EDGE,"E484.bottom"),sQuery(id+"F0.wireOp",EDGE,"E484.top"),sQuery(id+"F0.wireOp",EDGE,"E484.left"),sQuery(id+"F0.wireOp",EDGE,"E484.right")])],"isStart":false});
            var sketch = newSketch(context, id + "F2", { "sketchPlane" : qUnion([Q0])});
            skLineSegment(sketch, "E485.bottom", {"start": v(-67.5, 49) * mm, "end": v(-57.5, 49) * mm});
            skLineSegment(sketch, "E485.top", {"start": v(-67.5, 39) * mm, "end": v(-57.5, 39) * mm});
            skLineSegment(sketch, "E485.left", {"start": v(-67.5, 49) * mm, "end": v(-67.5, 39) * mm});
            skLineSegment(sketch, "E485.right", {"start": v(-57.5, 49) * mm, "end": v(-57.5, 39) * mm});
            skLineSegment(sketch, "E486.bottom", {"start": v(-67.5, -49) * mm, "end": v(-57.5, -49) * mm});
            skLineSegment(sketch, "E486.top", {"start": v(-67.5, -39) * mm, "end": v(-57.5, -39) * mm});
            skLineSegment(sketch, "E486.left", {"start": v(-67.5, -49) * mm, "end": v(-67.5, -39) * mm});
            skLineSegment(sketch, "E486.right", {"start": v(-57.5, -49) * mm, "end": v(-57.5, -39) * mm});
            skLineSegment(sketch, "E487.bottom", {"start": v(67.5, 49) * mm, "end": v(57.5, 49) * mm});
            skLineSegment(sketch, "E487.top", {"start": v(67.5, 39) * mm, "end": v(57.5, 39) * mm});
            skLineSegment(sketch, "E487.left", {"start": v(67.5, 49) * mm, "end": v(67.5, 39) * mm});
            skLineSegment(sketch, "E487.right", {"start": v(57.5, 49) * mm, "end": v(57.5, 39) * mm});
            skLineSegment(sketch, "E488.bottom", {"start": v(67.5, -49) * mm, "end": v(57.5, -49) * mm});
            skLineSegment(sketch, "E488.top", {"start": v(67.5, -39) * mm, "end": v(57.5, -39) * mm});
            skLineSegment(sketch, "E488.left", {"start": v(67.5, -49) * mm, "end": v(67.5, -39) * mm});
            skLineSegment(sketch, "E488.right", {"start": v(57.5, -49) * mm, "end": v(57.5, -39) * mm});
            skSolve(sketch);
        }
        {
            var Q0;
            Q0=makeQuery(id+"F2.imprint","IMPRINT",FACE,{"disambiguationData":[TD([[makeQuery(id+"F2.imprint","IMPRINT",EDGE,{"derivedFrom":sQuery(id+"F2.wireOp",EDGE,"E485.bottom")}),1.0]])]});
            var Q1;
            Q1=makeQuery(id+"F2.imprint","IMPRINT",FACE,{"disambiguationData":[TD([[makeQuery(id+"F2.imprint","IMPRINT",EDGE,{"derivedFrom":sQuery(id+"F2.wireOp",EDGE,"E486.bottom")}),-1.0]])]});
            var Q2;
            Q2=makeQuery(id+"F2.imprint","IMPRINT",FACE,{"disambiguationData":[TD([[makeQuery(id+"F2.imprint","IMPRINT",EDGE,{"derivedFrom":sQuery(id+"F2.wireOp",EDGE,"E488.bottom")}),-1.0]])]});
            var Q3;
            Q3=makeQuery(id+"F2.imprint","IMPRINT",FACE,{"disambiguationData":[TD([[makeQuery(id+"F2.imprint","IMPRINT",EDGE,{"derivedFrom":sQuery(id+"F2.wireOp",EDGE,"E487.bottom")}),1.0]])]});
            extrude(context, id + "F3", {"entities" : qUnion([Q0, Q1, Q2, Q3]), "operationType" : NewBodyOperationType.ADD, "depth" : 10 * mm, "offsetDistance" : 25 * mm});
        }
        {
            var Q0;
            Q0=makeQuery(id+"F1.opExtrude","CAP_FACE",FACE,{"disambiguationData":[OSD([sQuery(id+"F0.wireOp",EDGE,"E4"),sQuery(id+"F0.wireOp",EDGE,"E5"),sQuery(id+"F0.wireOp",EDGE,"E6"),sQuery(id+"F0.wireOp",EDGE,"E7"),sQuery(id+"F0.wireOp",EDGE,"E8"),sQuery(id+"F0.wireOp",EDGE,"E9"),sQuery(id+"F0.wireOp",EDGE,"E10"),sQuery(id+"F0.wireOp",EDGE,"E11"),sQuery(id+"F0.wireOp",EDGE,"E12"),sQuery(id+"F0.wireOp",EDGE,"E13"),sQuery(id+"F0.wireOp",EDGE,"E14"),sQuery(id+"F0.wireOp",EDGE,"E15"),sQuery(id+"F0.wireOp",EDGE,"E16"),sQuery(id+"F0.wireOp",EDGE,"E17"),sQuery(id+"F0.wireOp",EDGE,"E18"),sQuery(id+"F0.wireOp",EDGE,"E19"),sQuery(id+"F0.wireOp",EDGE,"E20"),sQuery(id+"F0.wireOp",EDGE,"E21"),sQuery(id+"F0.wireOp",EDGE,"E22"),sQuery(id+"F0.wireOp",EDGE,"E23"),sQuery(id+"F0.wireOp",EDGE,"E24"),sQuery(id+"F0.wireOp",EDGE,"E25"),sQuery(id+"F0.wireOp",EDGE,"E26"),sQuery(id+"F0.wireOp",EDGE,"E27"),sQuery(id+"F0.wireOp",EDGE,"E28"),sQuery(id+"F0.wireOp",EDGE,"E29"),sQuery(id+"F0.wireOp",EDGE,"E30"),sQuery(id+"F0.wireOp",EDGE,"E31"),sQuery(id+"F0.wireOp",EDGE,"E32"),sQuery(id+"F0.wireOp",EDGE,"E33"),sQuery(id+"F0.wireOp",EDGE,"E34"),sQuery(id+"F0.wireOp",EDGE,"E35"),sQuery(id+"F0.wireOp",EDGE,"E36"),sQuery(id+"F0.wireOp",EDGE,"E37"),sQuery(id+"F0.wireOp",EDGE,"E38"),sQuery(id+"F0.wireOp",EDGE,"E39"),sQuery(id+"F0.wireOp",EDGE,"E40"),sQuery(id+"F0.wireOp",EDGE,"E41"),sQuery(id+"F0.wireOp",EDGE,"E42"),sQuery(id+"F0.wireOp",EDGE,"E43"),sQuery(id+"F0.wireOp",EDGE,"E44"),sQuery(id+"F0.wireOp",EDGE,"E45"),sQuery(id+"F0.wireOp",EDGE,"E46"),sQuery(id+"F0.wireOp",EDGE,"E47"),sQuery(id+"F0.wireOp",EDGE,"E48"),sQuery(id+"F0.wireOp",EDGE,"E49"),sQuery(id+"F0.wireOp",EDGE,"E50"),sQuery(id+"F0.wireOp",EDGE,"E51"),sQuery(id+"F0.wireOp",EDGE,"E52"),sQuery(id+"F0.wireOp",EDGE,"E53"),sQuery(id+"F0.wireOp",EDGE,"E54"),sQuery(id+"F0.wireOp",EDGE,"E55"),sQuery(id+"F0.wireOp",EDGE,"E56"),sQuery(id+"F0.wireOp",EDGE,"E57"),sQuery(id+"F0.wireOp",EDGE,"E58"),sQuery(id+"F0.wireOp",EDGE,"E59"),sQuery(id+"F0.wireOp",EDGE,"E60"),sQuery(id+"F0.wireOp",EDGE,"E61"),sQuery(id+"F0.wireOp",EDGE,"E62"),sQuery(id+"F0.wireOp",EDGE,"E63"),sQuery(id+"F0.wireOp",EDGE,"E64"),sQuery(id+"F0.wireOp",EDGE,"E65"),sQuery(id+"F0.wireOp",EDGE,"E66"),sQuery(id+"F0.wireOp",EDGE,"E67"),sQuery(id+"F0.wireOp",EDGE,"E68"),sQuery(id+"F0.wireOp",EDGE,"E69"),sQuery(id+"F0.wireOp",EDGE,"E70"),sQuery(id+"F0.wireOp",EDGE,"E71"),sQuery(id+"F0.wireOp",EDGE,"E72"),sQuery(id+"F0.wireOp",EDGE,"E73"),sQuery(id+"F0.wireOp",EDGE,"E74"),sQuery(id+"F0.wireOp",EDGE,"E75"),sQuery(id+"F0.wireOp",EDGE,"E76"),sQuery(id+"F0.wireOp",EDGE,"E77"),sQuery(id+"F0.wireOp",EDGE,"E78"),sQuery(id+"F0.wireOp",EDGE,"E79"),sQuery(id+"F0.wireOp",EDGE,"E80"),sQuery(id+"F0.wireOp",EDGE,"E81"),sQuery(id+"F0.wireOp",EDGE,"E82"),sQuery(id+"F0.wireOp",EDGE,"E83"),sQuery(id+"F0.wireOp",EDGE,"E84"),sQuery(id+"F0.wireOp",EDGE,"E85"),sQuery(id+"F0.wireOp",EDGE,"E86"),sQuery(id+"F0.wireOp",EDGE,"E87"),sQuery(id+"F0.wireOp",EDGE,"E88"),sQuery(id+"F0.wireOp",EDGE,"E89"),sQuery(id+"F0.wireOp",EDGE,"E90"),sQuery(id+"F0.wireOp",EDGE,"E91"),sQuery(id+"F0.wireOp",EDGE,"E92"),sQuery(id+"F0.wireOp",EDGE,"E93"),sQuery(id+"F0.wireOp",EDGE,"E94"),sQuery(id+"F0.wireOp",EDGE,"E95"),sQuery(id+"F0.wireOp",EDGE,"E96"),sQuery(id+"F0.wireOp",EDGE,"E97"),sQuery(id+"F0.wireOp",EDGE,"E98"),sQuery(id+"F0.wireOp",EDGE,"E99"),sQuery(id+"F0.wireOp",EDGE,"E100"),sQuery(id+"F0.wireOp",EDGE,"E101"),sQuery(id+"F0.wireOp",EDGE,"E102"),sQuery(id+"F0.wireOp",EDGE,"E103"),sQuery(id+"F0.wireOp",EDGE,"E104"),sQuery(id+"F0.wireOp",EDGE,"E105"),sQuery(id+"F0.wireOp",EDGE,"E106"),sQuery(id+"F0.wireOp",EDGE,"E107"),sQuery(id+"F0.wireOp",EDGE,"E108"),sQuery(id+"F0.wireOp",EDGE,"E109"),sQuery(id+"F0.wireOp",EDGE,"E110"),sQuery(id+"F0.wireOp",EDGE,"E111"),sQuery(id+"F0.wireOp",EDGE,"E112"),sQuery(id+"F0.wireOp",EDGE,"E113"),sQuery(id+"F0.wireOp",EDGE,"E114"),sQuery(id+"F0.wireOp",EDGE,"E115"),sQuery(id+"F0.wireOp",EDGE,"E116"),sQuery(id+"F0.wireOp",EDGE,"E117"),sQuery(id+"F0.wireOp",EDGE,"E118"),sQuery(id+"F0.wireOp",EDGE,"E119"),sQuery(id+"F0.wireOp",EDGE,"E120"),sQuery(id+"F0.wireOp",EDGE,"E121"),sQuery(id+"F0.wireOp",EDGE,"E122"),sQuery(id+"F0.wireOp",EDGE,"E123"),sQuery(id+"F0.wireOp",EDGE,"E124"),sQuery(id+"F0.wireOp",EDGE,"E125"),sQuery(id+"F0.wireOp",EDGE,"E126"),sQuery(id+"F0.wireOp",EDGE,"E127"),sQuery(id+"F0.wireOp",EDGE,"E128"),sQuery(id+"F0.wireOp",EDGE,"E129"),sQuery(id+"F0.wireOp",EDGE,"E130"),sQuery(id+"F0.wireOp",EDGE,"E131"),sQuery(id+"F0.wireOp",EDGE,"E132"),sQuery(id+"F0.wireOp",EDGE,"E133"),sQuery(id+"F0.wireOp",EDGE,"E134"),sQuery(id+"F0.wireOp",EDGE,"E135"),sQuery(id+"F0.wireOp",EDGE,"E136"),sQuery(id+"F0.wireOp",EDGE,"E137"),sQuery(id+"F0.wireOp",EDGE,"E138"),sQuery(id+"F0.wireOp",EDGE,"E139"),sQuery(id+"F0.wireOp",EDGE,"E140"),sQuery(id+"F0.wireOp",EDGE,"E141"),sQuery(id+"F0.wireOp",EDGE,"E142"),sQuery(id+"F0.wireOp",EDGE,"E143"),sQuery(id+"F0.wireOp",EDGE,"E144"),sQuery(id+"F0.wireOp",EDGE,"E145"),sQuery(id+"F0.wireOp",EDGE,"E146"),sQuery(id+"F0.wireOp",EDGE,"E147"),sQuery(id+"F0.wireOp",EDGE,"E148"),sQuery(id+"F0.wireOp",EDGE,"E149"),sQuery(id+"F0.wireOp",EDGE,"E150"),sQuery(id+"F0.wireOp",EDGE,"E151"),sQuery(id+"F0.wireOp",EDGE,"E152"),sQuery(id+"F0.wireOp",EDGE,"E153"),sQuery(id+"F0.wireOp",EDGE,"E154"),sQuery(id+"F0.wireOp",EDGE,"E155"),sQuery(id+"F0.wireOp",EDGE,"E156"),sQuery(id+"F0.wireOp",EDGE,"E157"),sQuery(id+"F0.wireOp",EDGE,"E158"),sQuery(id+"F0.wireOp",EDGE,"E159"),sQuery(id+"F0.wireOp",EDGE,"E160"),sQuery(id+"F0.wireOp",EDGE,"E161"),sQuery(id+"F0.wireOp",EDGE,"E162"),sQuery(id+"F0.wireOp",EDGE,"E163"),sQuery(id+"F0.wireOp",EDGE,"E164"),sQuery(id+"F0.wireOp",EDGE,"E165"),sQuery(id+"F0.wireOp",EDGE,"E166"),sQuery(id+"F0.wireOp",EDGE,"E167"),sQuery(id+"F0.wireOp",EDGE,"E168"),sQuery(id+"F0.wireOp",EDGE,"E169"),sQuery(id+"F0.wireOp",EDGE,"E170"),sQuery(id+"F0.wireOp",EDGE,"E171"),sQuery(id+"F0.wireOp",EDGE,"E172"),sQuery(id+"F0.wireOp",EDGE,"E173"),sQuery(id+"F0.wireOp",EDGE,"E174"),sQuery(id+"F0.wireOp",EDGE,"E175"),sQuery(id+"F0.wireOp",EDGE,"E176"),sQuery(id+"F0.wireOp",EDGE,"E177"),sQuery(id+"F0.wireOp",EDGE,"E178"),sQuery(id+"F0.wireOp",EDGE,"E179"),sQuery(id+"F0.wireOp",EDGE,"E180"),sQuery(id+"F0.wireOp",EDGE,"E181"),sQuery(id+"F0.wireOp",EDGE,"E182"),sQuery(id+"F0.wireOp",EDGE,"E183"),sQuery(id+"F0.wireOp",EDGE,"E184"),sQuery(id+"F0.wireOp",EDGE,"E185"),sQuery(id+"F0.wireOp",EDGE,"E186"),sQuery(id+"F0.wireOp",EDGE,"E187"),sQuery(id+"F0.wireOp",EDGE,"E188"),sQuery(id+"F0.wireOp",EDGE,"E189"),sQuery(id+"F0.wireOp",EDGE,"E190"),sQuery(id+"F0.wireOp",EDGE,"E191"),sQuery(id+"F0.wireOp",EDGE,"E192"),sQuery(id+"F0.wireOp",EDGE,"E193"),sQuery(id+"F0.wireOp",EDGE,"E194"),sQuery(id+"F0.wireOp",EDGE,"E195"),sQuery(id+"F0.wireOp",EDGE,"E196"),sQuery(id+"F0.wireOp",EDGE,"E197"),sQuery(id+"F0.wireOp",EDGE,"E198"),sQuery(id+"F0.wireOp",EDGE,"E199"),sQuery(id+"F0.wireOp",EDGE,"E200"),sQuery(id+"F0.wireOp",EDGE,"E201"),sQuery(id+"F0.wireOp",EDGE,"E202"),sQuery(id+"F0.wireOp",EDGE,"E203"),sQuery(id+"F0.wireOp",EDGE,"E204"),sQuery(id+"F0.wireOp",EDGE,"E205"),sQuery(id+"F0.wireOp",EDGE,"E206"),sQuery(id+"F0.wireOp",EDGE,"E207"),sQuery(id+"F0.wireOp",EDGE,"E208"),sQuery(id+"F0.wireOp",EDGE,"E209"),sQuery(id+"F0.wireOp",EDGE,"E210"),sQuery(id+"F0.wireOp",EDGE,"E211"),sQuery(id+"F0.wireOp",EDGE,"E212"),sQuery(id+"F0.wireOp",EDGE,"E213"),sQuery(id+"F0.wireOp",EDGE,"E214"),sQuery(id+"F0.wireOp",EDGE,"E215"),sQuery(id+"F0.wireOp",EDGE,"E216"),sQuery(id+"F0.wireOp",EDGE,"E217"),sQuery(id+"F0.wireOp",EDGE,"E218"),sQuery(id+"F0.wireOp",EDGE,"E219"),sQuery(id+"F0.wireOp",EDGE,"E220"),sQuery(id+"F0.wireOp",EDGE,"E221"),sQuery(id+"F0.wireOp",EDGE,"E222"),sQuery(id+"F0.wireOp",EDGE,"E223"),sQuery(id+"F0.wireOp",EDGE,"E224"),sQuery(id+"F0.wireOp",EDGE,"E225"),sQuery(id+"F0.wireOp",EDGE,"E226"),sQuery(id+"F0.wireOp",EDGE,"E227"),sQuery(id+"F0.wireOp",EDGE,"E228"),sQuery(id+"F0.wireOp",EDGE,"E229"),sQuery(id+"F0.wireOp",EDGE,"E230"),sQuery(id+"F0.wireOp",EDGE,"E231"),sQuery(id+"F0.wireOp",EDGE,"E232"),sQuery(id+"F0.wireOp",EDGE,"E233"),sQuery(id+"F0.wireOp",EDGE,"E234"),sQuery(id+"F0.wireOp",EDGE,"E235"),sQuery(id+"F0.wireOp",EDGE,"E236"),sQuery(id+"F0.wireOp",EDGE,"E237"),sQuery(id+"F0.wireOp",EDGE,"E238"),sQuery(id+"F0.wireOp",EDGE,"E239"),sQuery(id+"F0.wireOp",EDGE,"E240"),sQuery(id+"F0.wireOp",EDGE,"E241"),sQuery(id+"F0.wireOp",EDGE,"E242"),sQuery(id+"F0.wireOp",EDGE,"E243"),sQuery(id+"F0.wireOp",EDGE,"E244"),sQuery(id+"F0.wireOp",EDGE,"E245"),sQuery(id+"F0.wireOp",EDGE,"E246"),sQuery(id+"F0.wireOp",EDGE,"E247"),sQuery(id+"F0.wireOp",EDGE,"E248"),sQuery(id+"F0.wireOp",EDGE,"E249"),sQuery(id+"F0.wireOp",EDGE,"E250"),sQuery(id+"F0.wireOp",EDGE,"E251"),sQuery(id+"F0.wireOp",EDGE,"E252"),sQuery(id+"F0.wireOp",EDGE,"E253"),sQuery(id+"F0.wireOp",EDGE,"E254"),sQuery(id+"F0.wireOp",EDGE,"E255"),sQuery(id+"F0.wireOp",EDGE,"E256"),sQuery(id+"F0.wireOp",EDGE,"E257"),sQuery(id+"F0.wireOp",EDGE,"E258"),sQuery(id+"F0.wireOp",EDGE,"E259"),sQuery(id+"F0.wireOp",EDGE,"E260"),sQuery(id+"F0.wireOp",EDGE,"E261"),sQuery(id+"F0.wireOp",EDGE,"E262"),sQuery(id+"F0.wireOp",EDGE,"E263"),sQuery(id+"F0.wireOp",EDGE,"E264"),sQuery(id+"F0.wireOp",EDGE,"E265"),sQuery(id+"F0.wireOp",EDGE,"E266"),sQuery(id+"F0.wireOp",EDGE,"E267"),sQuery(id+"F0.wireOp",EDGE,"E268"),sQuery(id+"F0.wireOp",EDGE,"E269"),sQuery(id+"F0.wireOp",EDGE,"E270"),sQuery(id+"F0.wireOp",EDGE,"E271"),sQuery(id+"F0.wireOp",EDGE,"E272"),sQuery(id+"F0.wireOp",EDGE,"E273"),sQuery(id+"F0.wireOp",EDGE,"E274"),sQuery(id+"F0.wireOp",EDGE,"E275"),sQuery(id+"F0.wireOp",EDGE,"E276"),sQuery(id+"F0.wireOp",EDGE,"E277"),sQuery(id+"F0.wireOp",EDGE,"E278"),sQuery(id+"F0.wireOp",EDGE,"E279"),sQuery(id+"F0.wireOp",EDGE,"E280"),sQuery(id+"F0.wireOp",EDGE,"E281"),sQuery(id+"F0.wireOp",EDGE,"E282"),sQuery(id+"F0.wireOp",EDGE,"E283"),sQuery(id+"F0.wireOp",EDGE,"E284"),sQuery(id+"F0.wireOp",EDGE,"E285"),sQuery(id+"F0.wireOp",EDGE,"E286"),sQuery(id+"F0.wireOp",EDGE,"E287"),sQuery(id+"F0.wireOp",EDGE,"E288"),sQuery(id+"F0.wireOp",EDGE,"E289"),sQuery(id+"F0.wireOp",EDGE,"E290"),sQuery(id+"F0.wireOp",EDGE,"E291"),sQuery(id+"F0.wireOp",EDGE,"E292"),sQuery(id+"F0.wireOp",EDGE,"E293"),sQuery(id+"F0.wireOp",EDGE,"E294"),sQuery(id+"F0.wireOp",EDGE,"E295"),sQuery(id+"F0.wireOp",EDGE,"E296"),sQuery(id+"F0.wireOp",EDGE,"E297"),sQuery(id+"F0.wireOp",EDGE,"E298"),sQuery(id+"F0.wireOp",EDGE,"E299"),sQuery(id+"F0.wireOp",EDGE,"E300"),sQuery(id+"F0.wireOp",EDGE,"E301"),sQuery(id+"F0.wireOp",EDGE,"E302"),sQuery(id+"F0.wireOp",EDGE,"E303"),sQuery(id+"F0.wireOp",EDGE,"E304"),sQuery(id+"F0.wireOp",EDGE,"E305"),sQuery(id+"F0.wireOp",EDGE,"E306"),sQuery(id+"F0.wireOp",EDGE,"E307"),sQuery(id+"F0.wireOp",EDGE,"E308"),sQuery(id+"F0.wireOp",EDGE,"E309"),sQuery(id+"F0.wireOp",EDGE,"E310"),sQuery(id+"F0.wireOp",EDGE,"E311"),sQuery(id+"F0.wireOp",EDGE,"E312"),sQuery(id+"F0.wireOp",EDGE,"E313"),sQuery(id+"F0.wireOp",EDGE,"E314"),sQuery(id+"F0.wireOp",EDGE,"E315"),sQuery(id+"F0.wireOp",EDGE,"E316"),sQuery(id+"F0.wireOp",EDGE,"E317"),sQuery(id+"F0.wireOp",EDGE,"E318"),sQuery(id+"F0.wireOp",EDGE,"E319"),sQuery(id+"F0.wireOp",EDGE,"E320"),sQuery(id+"F0.wireOp",EDGE,"E321"),sQuery(id+"F0.wireOp",EDGE,"E322"),sQuery(id+"F0.wireOp",EDGE,"E323"),sQuery(id+"F0.wireOp",EDGE,"E324"),sQuery(id+"F0.wireOp",EDGE,"E325"),sQuery(id+"F0.wireOp",EDGE,"E326"),sQuery(id+"F0.wireOp",EDGE,"E327"),sQuery(id+"F0.wireOp",EDGE,"E328"),sQuery(id+"F0.wireOp",EDGE,"E329"),sQuery(id+"F0.wireOp",EDGE,"E330"),sQuery(id+"F0.wireOp",EDGE,"E331"),sQuery(id+"F0.wireOp",EDGE,"E332"),sQuery(id+"F0.wireOp",EDGE,"E333"),sQuery(id+"F0.wireOp",EDGE,"E334"),sQuery(id+"F0.wireOp",EDGE,"E335"),sQuery(id+"F0.wireOp",EDGE,"E336"),sQuery(id+"F0.wireOp",EDGE,"E337"),sQuery(id+"F0.wireOp",EDGE,"E338"),sQuery(id+"F0.wireOp",EDGE,"E339"),sQuery(id+"F0.wireOp",EDGE,"E340"),sQuery(id+"F0.wireOp",EDGE,"E341"),sQuery(id+"F0.wireOp",EDGE,"E342"),sQuery(id+"F0.wireOp",EDGE,"E343"),sQuery(id+"F0.wireOp",EDGE,"E344"),sQuery(id+"F0.wireOp",EDGE,"E345"),sQuery(id+"F0.wireOp",EDGE,"E346"),sQuery(id+"F0.wireOp",EDGE,"E347"),sQuery(id+"F0.wireOp",EDGE,"E348"),sQuery(id+"F0.wireOp",EDGE,"E349"),sQuery(id+"F0.wireOp",EDGE,"E350"),sQuery(id+"F0.wireOp",EDGE,"E351"),sQuery(id+"F0.wireOp",EDGE,"E352"),sQuery(id+"F0.wireOp",EDGE,"E353"),sQuery(id+"F0.wireOp",EDGE,"E354"),sQuery(id+"F0.wireOp",EDGE,"E355"),sQuery(id+"F0.wireOp",EDGE,"E356"),sQuery(id+"F0.wireOp",EDGE,"E357"),sQuery(id+"F0.wireOp",EDGE,"E358"),sQuery(id+"F0.wireOp",EDGE,"E359"),sQuery(id+"F0.wireOp",EDGE,"E360"),sQuery(id+"F0.wireOp",EDGE,"E361"),sQuery(id+"F0.wireOp",EDGE,"E362"),sQuery(id+"F0.wireOp",EDGE,"E363"),sQuery(id+"F0.wireOp",EDGE,"E364"),sQuery(id+"F0.wireOp",EDGE,"E365"),sQuery(id+"F0.wireOp",EDGE,"E366"),sQuery(id+"F0.wireOp",EDGE,"E367"),sQuery(id+"F0.wireOp",EDGE,"E368"),sQuery(id+"F0.wireOp",EDGE,"E369"),sQuery(id+"F0.wireOp",EDGE,"E370"),sQuery(id+"F0.wireOp",EDGE,"E371"),sQuery(id+"F0.wireOp",EDGE,"E372"),sQuery(id+"F0.wireOp",EDGE,"E373"),sQuery(id+"F0.wireOp",EDGE,"E374"),sQuery(id+"F0.wireOp",EDGE,"E375"),sQuery(id+"F0.wireOp",EDGE,"E376"),sQuery(id+"F0.wireOp",EDGE,"E377"),sQuery(id+"F0.wireOp",EDGE,"E378"),sQuery(id+"F0.wireOp",EDGE,"E379"),sQuery(id+"F0.wireOp",EDGE,"E380"),sQuery(id+"F0.wireOp",EDGE,"E381"),sQuery(id+"F0.wireOp",EDGE,"E382"),sQuery(id+"F0.wireOp",EDGE,"E383"),sQuery(id+"F0.wireOp",EDGE,"E384"),sQuery(id+"F0.wireOp",EDGE,"E385"),sQuery(id+"F0.wireOp",EDGE,"E386"),sQuery(id+"F0.wireOp",EDGE,"E387"),sQuery(id+"F0.wireOp",EDGE,"E388"),sQuery(id+"F0.wireOp",EDGE,"E389"),sQuery(id+"F0.wireOp",EDGE,"E390"),sQuery(id+"F0.wireOp",EDGE,"E391"),sQuery(id+"F0.wireOp",EDGE,"E392"),sQuery(id+"F0.wireOp",EDGE,"E393"),sQuery(id+"F0.wireOp",EDGE,"E394"),sQuery(id+"F0.wireOp",EDGE,"E395"),sQuery(id+"F0.wireOp",EDGE,"E396"),sQuery(id+"F0.wireOp",EDGE,"E397"),sQuery(id+"F0.wireOp",EDGE,"E398"),sQuery(id+"F0.wireOp",EDGE,"E399"),sQuery(id+"F0.wireOp",EDGE,"E400"),sQuery(id+"F0.wireOp",EDGE,"E401"),sQuery(id+"F0.wireOp",EDGE,"E402"),sQuery(id+"F0.wireOp",EDGE,"E403"),sQuery(id+"F0.wireOp",EDGE,"E404"),sQuery(id+"F0.wireOp",EDGE,"E405"),sQuery(id+"F0.wireOp",EDGE,"E406"),sQuery(id+"F0.wireOp",EDGE,"E407"),sQuery(id+"F0.wireOp",EDGE,"E408"),sQuery(id+"F0.wireOp",EDGE,"E409"),sQuery(id+"F0.wireOp",EDGE,"E410"),sQuery(id+"F0.wireOp",EDGE,"E411"),sQuery(id+"F0.wireOp",EDGE,"E412"),sQuery(id+"F0.wireOp",EDGE,"E413"),sQuery(id+"F0.wireOp",EDGE,"E414"),sQuery(id+"F0.wireOp",EDGE,"E415"),sQuery(id+"F0.wireOp",EDGE,"E416"),sQuery(id+"F0.wireOp",EDGE,"E417"),sQuery(id+"F0.wireOp",EDGE,"E418"),sQuery(id+"F0.wireOp",EDGE,"E419"),sQuery(id+"F0.wireOp",EDGE,"E420"),sQuery(id+"F0.wireOp",EDGE,"E421"),sQuery(id+"F0.wireOp",EDGE,"E422"),sQuery(id+"F0.wireOp",EDGE,"E423"),sQuery(id+"F0.wireOp",EDGE,"E424"),sQuery(id+"F0.wireOp",EDGE,"E425"),sQuery(id+"F0.wireOp",EDGE,"E426"),sQuery(id+"F0.wireOp",EDGE,"E427"),sQuery(id+"F0.wireOp",EDGE,"E428"),sQuery(id+"F0.wireOp",EDGE,"E429"),sQuery(id+"F0.wireOp",EDGE,"E430"),sQuery(id+"F0.wireOp",EDGE,"E431"),sQuery(id+"F0.wireOp",EDGE,"E432"),sQuery(id+"F0.wireOp",EDGE,"E433"),sQuery(id+"F0.wireOp",EDGE,"E434"),sQuery(id+"F0.wireOp",EDGE,"E435"),sQuery(id+"F0.wireOp",EDGE,"E436"),sQuery(id+"F0.wireOp",EDGE,"E437"),sQuery(id+"F0.wireOp",EDGE,"E438"),sQuery(id+"F0.wireOp",EDGE,"E439"),sQuery(id+"F0.wireOp",EDGE,"E440"),sQuery(id+"F0.wireOp",EDGE,"E441"),sQuery(id+"F0.wireOp",EDGE,"E442"),sQuery(id+"F0.wireOp",EDGE,"E443"),sQuery(id+"F0.wireOp",EDGE,"E444"),sQuery(id+"F0.wireOp",EDGE,"E445"),sQuery(id+"F0.wireOp",EDGE,"E446"),sQuery(id+"F0.wireOp",EDGE,"E447"),sQuery(id+"F0.wireOp",EDGE,"E448"),sQuery(id+"F0.wireOp",EDGE,"E449"),sQuery(id+"F0.wireOp",EDGE,"E450"),sQuery(id+"F0.wireOp",EDGE,"E451"),sQuery(id+"F0.wireOp",EDGE,"E452"),sQuery(id+"F0.wireOp",EDGE,"E453"),sQuery(id+"F0.wireOp",EDGE,"E454"),sQuery(id+"F0.wireOp",EDGE,"E455"),sQuery(id+"F0.wireOp",EDGE,"E456"),sQuery(id+"F0.wireOp",EDGE,"E457"),sQuery(id+"F0.wireOp",EDGE,"E458"),sQuery(id+"F0.wireOp",EDGE,"E459"),sQuery(id+"F0.wireOp",EDGE,"E460"),sQuery(id+"F0.wireOp",EDGE,"E461"),sQuery(id+"F0.wireOp",EDGE,"E462"),sQuery(id+"F0.wireOp",EDGE,"E463"),sQuery(id+"F0.wireOp",EDGE,"E464"),sQuery(id+"F0.wireOp",EDGE,"E465"),sQuery(id+"F0.wireOp",EDGE,"E466"),sQuery(id+"F0.wireOp",EDGE,"E467"),sQuery(id+"F0.wireOp",EDGE,"E468"),sQuery(id+"F0.wireOp",EDGE,"E469"),sQuery(id+"F0.wireOp",EDGE,"E470"),sQuery(id+"F0.wireOp",EDGE,"E471"),sQuery(id+"F0.wireOp",EDGE,"E472"),sQuery(id+"F0.wireOp",EDGE,"E473"),sQuery(id+"F0.wireOp",EDGE,"E474"),sQuery(id+"F0.wireOp",EDGE,"E475"),sQuery(id+"F0.wireOp",EDGE,"E476"),sQuery(id+"F0.wireOp",EDGE,"E477"),sQuery(id+"F0.wireOp",EDGE,"E478"),sQuery(id+"F0.wireOp",EDGE,"E479"),sQuery(id+"F0.wireOp",EDGE,"E480"),sQuery(id+"F0.wireOp",EDGE,"E481"),sQuery(id+"F0.wireOp",EDGE,"E482"),sQuery(id+"F0.wireOp",EDGE,"E483"),sQuery(id+"F0.wireOp",EDGE,"E484.bottom"),sQuery(id+"F0.wireOp",EDGE,"E484.top"),sQuery(id+"F0.wireOp",EDGE,"E484.left"),sQuery(id+"F0.wireOp",EDGE,"E484.right")])],"isStart":false});
            var sketch = newSketch(context, id + "F4", { "sketchPlane" : qUnion([Q0])});
            skLineSegment(sketch, "E489.bottom", {"start": v(-57.5, -49) * mm, "end": v(57.5, -49) * mm});
            skLineSegment(sketch, "E489.top", {"start": v(-57.5, -39) * mm, "end": v(57.5, -39) * mm});
            skLineSegment(sketch, "E489.left", {"start": v(-57.5, -49) * mm, "end": v(-57.5, -39) * mm});
            skLineSegment(sketch, "E489.right", {"start": v(57.5, -49) * mm, "end": v(57.5, -39) * mm});
            skLineSegment(sketch, "E490.bottom", {"start": v(57.5, 39) * mm, "end": v(67.5, 39) * mm});
            skLineSegment(sketch, "E490.top", {"start": v(57.5, -39) * mm, "end": v(67.5, -39) * mm});
            skLineSegment(sketch, "E490.left", {"start": v(57.5, 39) * mm, "end": v(57.5, -39) * mm});
            skLineSegment(sketch, "E490.right", {"start": v(67.5, 39) * mm, "end": v(67.5, -39) * mm});
            skLineSegment(sketch, "E491.bottom", {"start": v(-57.5, 49) * mm, "end": v(57.5, 49) * mm});
            skLineSegment(sketch, "E491.top", {"start": v(-57.5, 39) * mm, "end": v(57.5, 39) * mm});
            skLineSegment(sketch, "E491.left", {"start": v(-57.5, 49) * mm, "end": v(-57.5, 39) * mm});
            skLineSegment(sketch, "E491.right", {"start": v(57.5, 49) * mm, "end": v(57.5, 39) * mm});
            skLineSegment(sketch, "E492.bottom", {"start": v(-67.5, 39) * mm, "end": v(-57.5, 39) * mm});
            skLineSegment(sketch, "E492.top", {"start": v(-67.5, -39) * mm, "end": v(-57.5, -39) * mm});
            skLineSegment(sketch, "E492.left", {"start": v(-67.5, 39) * mm, "end": v(-67.5, -39) * mm});
            skLineSegment(sketch, "E492.right", {"start": v(-57.5, 39) * mm, "end": v(-57.5, -39) * mm});
            skSolve(sketch);
        }
        {
            var Q0;
            Q0=makeQuery(id+"F4.imprint","IMPRINT",FACE,{"disambiguationData":[TD([[makeQuery(id+"F4.imprint","IMPRINT",EDGE,{"derivedFrom":sQuery(id+"F4.wireOp",EDGE,"E492.bottom")}),-1.0]])]});
            var Q1;
            Q1=makeQuery(id+"F4.imprint","IMPRINT",FACE,{"disambiguationData":[TD([[makeQuery(id+"F4.imprint","IMPRINT",EDGE,{"derivedFrom":sQuery(id+"F4.wireOp",EDGE,"E491.bottom")}),1.0]])]});
            var Q2;
            Q2=makeQuery(id+"F4.imprint","IMPRINT",FACE,{"disambiguationData":[TD([[makeQuery(id+"F4.imprint","IMPRINT",EDGE,{"derivedFrom":sQuery(id+"F4.wireOp",EDGE,"E490.bottom")}),1.0]])]});
            var Q3;
            Q3=makeQuery(id+"F4.imprint","IMPRINT",FACE,{"disambiguationData":[TD([[makeQuery(id+"F4.imprint","IMPRINT",EDGE,{"derivedFrom":sQuery(id+"F4.wireOp",EDGE,"E489.bottom")}),-1.0]])]});
            extrude(context, id + "F5", {"entities" : qUnion([Q0, Q1, Q2, Q3]), "operationType" : NewBodyOperationType.ADD, "depth" : 5 * mm, "offsetDistance" : 25 * mm});
        }
    });
